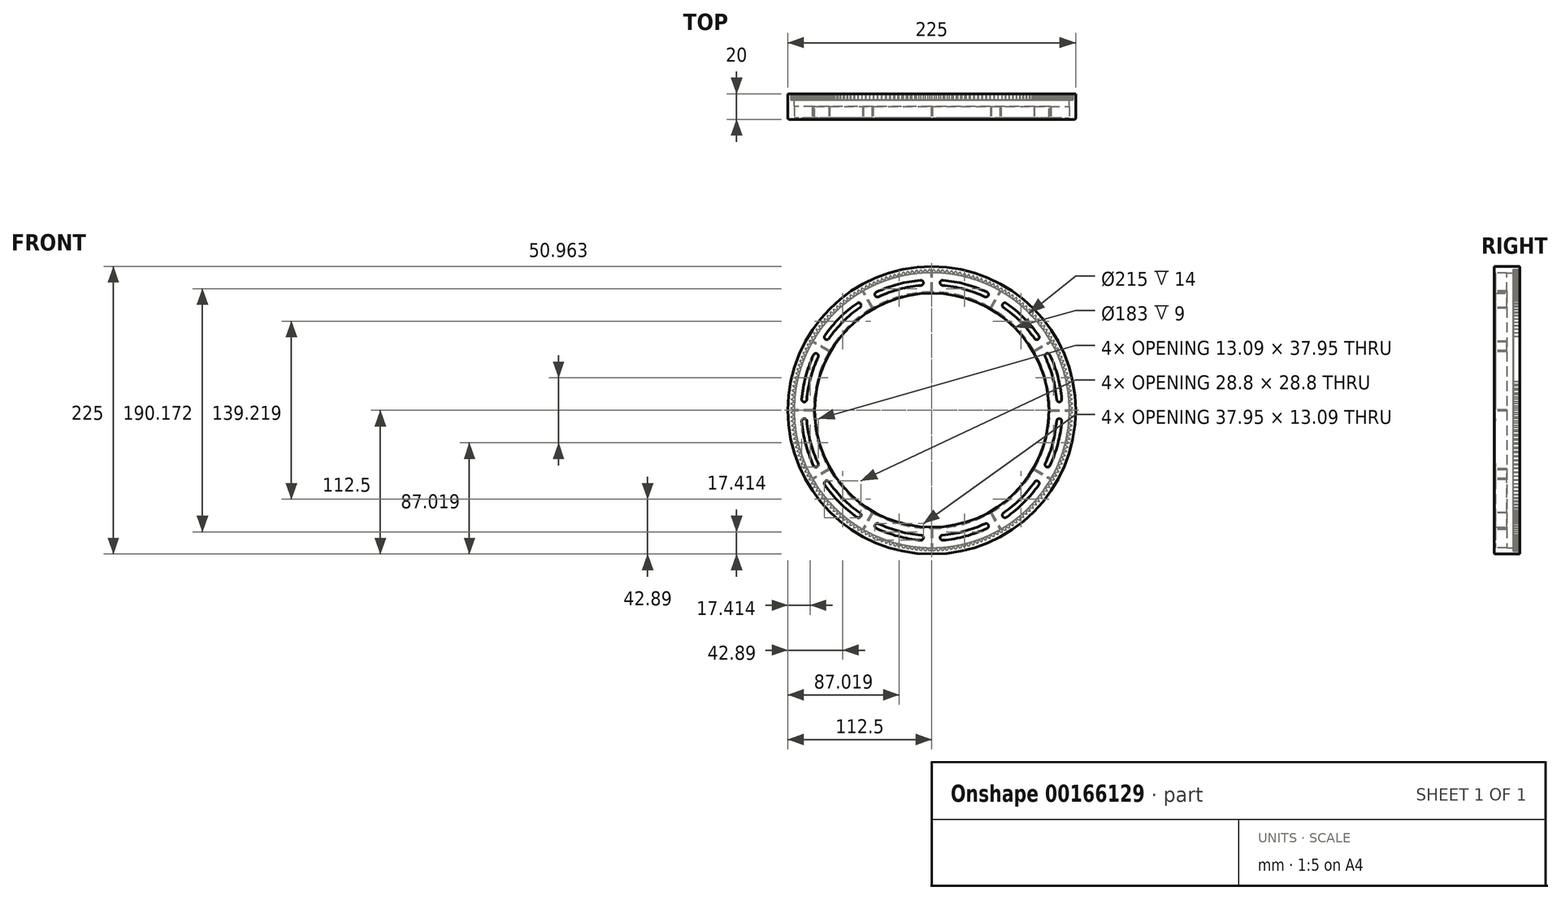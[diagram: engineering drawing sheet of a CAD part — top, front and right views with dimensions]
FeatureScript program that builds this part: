
annotation { "Feature Type Name" : "Feature", "Feature Type Description" : "" }
export const myFeature = defineFeature(function(context is Context, id is Id, definition is map)
    precondition{}
    {
        {
            var Q0;
            Q0=qCreatedBy(makeId("Top.planeOp"),FACE);
            var sketch = newSketch(context, id + "F0", { "sketchPlane" : qUnion([Q0])});
            skLineSegment(sketch, "E0", {"start": v(0, 14) * mm, "end": v(0, 0) * mm});
            skLineSegment(sketch, "E1", {"start": v(0, 14) * mm, "end": v(5, 14) * mm});
            skLineSegment(sketch, "E2", {"start": v(5, 14) * mm, "end": v(5, 0) * mm});
            skLineSegment(sketch, "E3", {"start": v(5, 0) * mm, "end": v(20, 0) * mm});
            skLineSegment(sketch, "E4", {"start": v(20, 0) * mm, "end": v(20, 9) * mm});
            skLineSegment(sketch, "E5", {"start": v(20, 9) * mm, "end": v(21, 9) * mm});
            skLineSegment(sketch, "E6", {"start": v(21, 9) * mm, "end": v(21, 0) * mm});
            skArc(sketch, "E7", {"start": v(0, 0) * mm, "mid": v(0.3, -0.7) * mm, "end": v(1, -1) * mm});
            skLineSegment(sketch, "E8", {"start": v(1, -1) * mm, "end": v(20, -1) * mm});
            skArc(sketch, "E9", {"start": v(21, 0) * mm, "mid": v(20.7, -0.7) * mm, "end": v(20, -1) * mm});
            skLineSegment(sketch, "E10", {"start": v(112.5, 10) * mm, "end": v(112.5, 0) * mm});
            skSolve(sketch);
        }
        {
            var Q0;
            Q0=makeQuery(id+"F0.imprint","IMPRINT",FACE,{"disambiguationData":[TD([[makeQuery(id+"F0.imprint","IMPRINT",EDGE,{"derivedFrom":sQuery(id+"F0.wireOp",EDGE,"E0")}),1.0]])]});
            var Q1;
            Q1=sQuery(id+"F0.wireOp",EDGE,"E10");
            revolve(context, id + "F1", {"entities" : qUnion([Q0]), "axis" : qUnion([Q1]), "revolveType" : RevolveType.FULL});
        }
        {
            var Q0;
            Q0=makeQuery(id+"F1.opRevolve","SWEPT_FACE",FACE,{"disambiguationData":[OSD([sQuery(id+"F0.wireOp",EDGE,"E3")])]});
            var sketch = newSketch(context, id + "F2", { "sketchPlane" : qUnion([Q0])});
            skLineSegment(sketch, "E11", {"start": v(-20, -0.5) * mm, "end": v(-5, -0.5) * mm});
            skLineSegment(sketch, "E12", {"start": v(-20, 0.5) * mm, "end": v(-5, 0.5) * mm});
            skPoint(sketch, "E13.start.orphan", {"position": v(-20, 0) * mm});
            skLineSegment(sketch, "E14.1.0", {"start": v(-32.64, 46.68) * mm, "end": v(-19.65, 54.18) * mm});
            skLineSegment(sketch, "E14.1.1", {"start": v(-32.14, 45.82) * mm, "end": v(-19.15, 53.32) * mm});
            skLineSegment(sketch, "E14.2.0", {"start": v(-66.68, 80.36) * mm, "end": v(-59.18, 93.35) * mm});
            skLineSegment(sketch, "E14.2.1", {"start": v(-65.82, 79.86) * mm, "end": v(-58.32, 92.85) * mm});
            skLineSegment(sketch, "E14.3.0", {"start": v(-113, 92.5) * mm, "end": v(-113, 107.5) * mm});
            skLineSegment(sketch, "E14.3.1", {"start": v(-112, 92.5) * mm, "end": v(-112, 107.5) * mm});
            skLineSegment(sketch, "E14.4.0", {"start": v(-159.18, 79.86) * mm, "end": v(-166.68, 92.85) * mm});
            skLineSegment(sketch, "E14.4.1", {"start": v(-158.32, 80.36) * mm, "end": v(-165.82, 93.35) * mm});
            skLineSegment(sketch, "E14.5.0", {"start": v(-192.86, 45.82) * mm, "end": v(-205.85, 53.32) * mm});
            skLineSegment(sketch, "E14.5.1", {"start": v(-192.36, 46.68) * mm, "end": v(-205.35, 54.18) * mm});
            skLineSegment(sketch, "E14.6.0", {"start": v(-205, -0.5) * mm, "end": v(-220, -0.5) * mm});
            skLineSegment(sketch, "E14.6.1", {"start": v(-205, 0.5) * mm, "end": v(-220, 0.5) * mm});
            skLineSegment(sketch, "E14.7.0", {"start": v(-192.36, -46.68) * mm, "end": v(-205.35, -54.18) * mm});
            skLineSegment(sketch, "E14.7.1", {"start": v(-192.86, -45.82) * mm, "end": v(-205.85, -53.32) * mm});
            skLineSegment(sketch, "E14.8.0", {"start": v(-158.32, -80.36) * mm, "end": v(-165.82, -93.35) * mm});
            skLineSegment(sketch, "E14.8.1", {"start": v(-159.18, -79.86) * mm, "end": v(-166.68, -92.85) * mm});
            skLineSegment(sketch, "E14.9.0", {"start": v(-112, -92.5) * mm, "end": v(-112, -107.5) * mm});
            skLineSegment(sketch, "E14.9.1", {"start": v(-113, -92.5) * mm, "end": v(-113, -107.5) * mm});
            skLineSegment(sketch, "E14.10.0", {"start": v(-65.82, -79.86) * mm, "end": v(-58.32, -92.85) * mm});
            skLineSegment(sketch, "E14.10.1", {"start": v(-66.68, -80.36) * mm, "end": v(-59.18, -93.35) * mm});
            skLineSegment(sketch, "E14.11.0", {"start": v(-32.14, -45.82) * mm, "end": v(-19.15, -53.32) * mm});
            skLineSegment(sketch, "E14.11.1", {"start": v(-32.64, -46.68) * mm, "end": v(-19.65, -54.18) * mm});
            skPoint(sketch, "E14.center", {"position": v(-112.5, 0) * mm});
            skArc(sketch, "E15.0.startCap", {"start": v(-210.15, 8.33) * mm, "mid": v(-212.3, 6.5) * mm, "end": v(-214.13, 8.67) * mm});
            skArc(sketch, "E15.0.endCap", {"start": v(-204.85, 43.3) * mm, "mid": v(-202.19, 44.27) * mm, "end": v(-201.23, 41.6) * mm});
            skArc(sketch, "E15.0.left", {"start": v(-214.13, 8.67) * mm, "mid": v(-211.02, 26.4) * mm, "end": v(-204.85, 43.3) * mm});
            skArc(sketch, "E15.0.right", {"start": v(-210.15, 8.33) * mm, "mid": v(-207.16, 25.36) * mm, "end": v(-201.23, 41.6) * mm});
            skArc(sketch, "E16.1.0", {"start": v(-201.23, -41.6) * mm, "mid": v(-207.16, -25.36) * mm, "end": v(-210.15, -8.33) * mm});
            skArc(sketch, "E16.1.1", {"start": v(-201.23, -41.6) * mm, "mid": v(-202.19, -44.27) * mm, "end": v(-204.85, -43.3) * mm});
            skArc(sketch, "E16.1.2", {"start": v(-204.85, -43.3) * mm, "mid": v(-211.02, -26.4) * mm, "end": v(-214.13, -8.67) * mm});
            skArc(sketch, "E16.1.3", {"start": v(-214.13, -8.67) * mm, "mid": v(-212.3, -6.5) * mm, "end": v(-210.15, -8.33) * mm});
            skArc(sketch, "E16.2.0", {"start": v(-168.54, -80.4) * mm, "mid": v(-181.8, -69.3) * mm, "end": v(-192.9, -56.04) * mm});
            skArc(sketch, "E16.2.1", {"start": v(-168.54, -80.4) * mm, "mid": v(-168.04, -83.18) * mm, "end": v(-170.82, -83.68) * mm});
            skArc(sketch, "E16.2.2", {"start": v(-170.82, -83.68) * mm, "mid": v(-184.62, -72.12) * mm, "end": v(-196.18, -58.32) * mm});
            skArc(sketch, "E16.2.3", {"start": v(-196.18, -58.32) * mm, "mid": v(-195.68, -55.54) * mm, "end": v(-192.9, -56.04) * mm});
            skArc(sketch, "E16.3.0", {"start": v(-120.83, -97.65) * mm, "mid": v(-137.86, -94.66) * mm, "end": v(-154.1, -88.73) * mm});
            skArc(sketch, "E16.3.1", {"start": v(-120.83, -97.65) * mm, "mid": v(-119, -99.8) * mm, "end": v(-121.17, -101.63) * mm});
            skArc(sketch, "E16.3.2", {"start": v(-121.17, -101.63) * mm, "mid": v(-138.9, -98.52) * mm, "end": v(-155.8, -92.35) * mm});
            skArc(sketch, "E16.3.3", {"start": v(-155.8, -92.35) * mm, "mid": v(-156.77, -89.69) * mm, "end": v(-154.1, -88.73) * mm});
            skArc(sketch, "E16.4.0", {"start": v(-70.9, -88.73) * mm, "mid": v(-87.14, -94.66) * mm, "end": v(-104.17, -97.65) * mm});
            skArc(sketch, "E16.4.1", {"start": v(-70.9, -88.73) * mm, "mid": v(-68.23, -89.69) * mm, "end": v(-69.2, -92.35) * mm});
            skArc(sketch, "E16.4.2", {"start": v(-69.2, -92.35) * mm, "mid": v(-86.1, -98.52) * mm, "end": v(-103.83, -101.63) * mm});
            skArc(sketch, "E16.4.3", {"start": v(-103.83, -101.63) * mm, "mid": v(-106, -99.8) * mm, "end": v(-104.17, -97.65) * mm});
            skArc(sketch, "E16.5.0", {"start": v(-32.1, -56.04) * mm, "mid": v(-43.2, -69.3) * mm, "end": v(-56.46, -80.4) * mm});
            skArc(sketch, "E16.5.1", {"start": v(-32.1, -56.04) * mm, "mid": v(-29.32, -55.54) * mm, "end": v(-28.82, -58.32) * mm});
            skArc(sketch, "E16.5.2", {"start": v(-28.82, -58.32) * mm, "mid": v(-40.38, -72.12) * mm, "end": v(-54.18, -83.68) * mm});
            skArc(sketch, "E16.5.3", {"start": v(-54.18, -83.68) * mm, "mid": v(-56.96, -83.18) * mm, "end": v(-56.46, -80.4) * mm});
            skArc(sketch, "E16.6.0", {"start": v(-14.85, -8.33) * mm, "mid": v(-17.84, -25.36) * mm, "end": v(-23.77, -41.6) * mm});
            skArc(sketch, "E16.6.1", {"start": v(-14.85, -8.33) * mm, "mid": v(-12.7, -6.5) * mm, "end": v(-10.87, -8.67) * mm});
            skArc(sketch, "E16.6.2", {"start": v(-10.87, -8.67) * mm, "mid": v(-13.98, -26.4) * mm, "end": v(-20.15, -43.3) * mm});
            skArc(sketch, "E16.6.3", {"start": v(-20.15, -43.3) * mm, "mid": v(-22.81, -44.27) * mm, "end": v(-23.77, -41.6) * mm});
            skArc(sketch, "E16.7.0", {"start": v(-23.77, 41.6) * mm, "mid": v(-17.84, 25.36) * mm, "end": v(-14.85, 8.33) * mm});
            skArc(sketch, "E16.7.1", {"start": v(-23.77, 41.6) * mm, "mid": v(-22.81, 44.27) * mm, "end": v(-20.15, 43.3) * mm});
            skArc(sketch, "E16.7.2", {"start": v(-20.15, 43.3) * mm, "mid": v(-13.98, 26.4) * mm, "end": v(-10.87, 8.67) * mm});
            skArc(sketch, "E16.7.3", {"start": v(-10.87, 8.67) * mm, "mid": v(-12.7, 6.5) * mm, "end": v(-14.85, 8.33) * mm});
            skArc(sketch, "E16.8.0", {"start": v(-56.46, 80.4) * mm, "mid": v(-43.2, 69.3) * mm, "end": v(-32.1, 56.04) * mm});
            skArc(sketch, "E16.8.1", {"start": v(-56.46, 80.4) * mm, "mid": v(-56.96, 83.18) * mm, "end": v(-54.18, 83.68) * mm});
            skArc(sketch, "E16.8.2", {"start": v(-54.18, 83.68) * mm, "mid": v(-40.38, 72.12) * mm, "end": v(-28.82, 58.32) * mm});
            skArc(sketch, "E16.8.3", {"start": v(-28.82, 58.32) * mm, "mid": v(-29.32, 55.54) * mm, "end": v(-32.1, 56.04) * mm});
            skArc(sketch, "E16.9.0", {"start": v(-104.17, 97.65) * mm, "mid": v(-87.14, 94.66) * mm, "end": v(-70.9, 88.73) * mm});
            skArc(sketch, "E16.9.1", {"start": v(-104.17, 97.65) * mm, "mid": v(-106, 99.8) * mm, "end": v(-103.83, 101.63) * mm});
            skArc(sketch, "E16.9.2", {"start": v(-103.83, 101.63) * mm, "mid": v(-86.1, 98.52) * mm, "end": v(-69.2, 92.35) * mm});
            skArc(sketch, "E16.9.3", {"start": v(-69.2, 92.35) * mm, "mid": v(-68.23, 89.69) * mm, "end": v(-70.9, 88.73) * mm});
            skArc(sketch, "E16.10.0", {"start": v(-154.1, 88.73) * mm, "mid": v(-137.86, 94.66) * mm, "end": v(-120.83, 97.65) * mm});
            skArc(sketch, "E16.10.1", {"start": v(-154.1, 88.73) * mm, "mid": v(-156.77, 89.69) * mm, "end": v(-155.8, 92.35) * mm});
            skArc(sketch, "E16.10.2", {"start": v(-155.8, 92.35) * mm, "mid": v(-138.9, 98.52) * mm, "end": v(-121.17, 101.63) * mm});
            skArc(sketch, "E16.10.3", {"start": v(-121.17, 101.63) * mm, "mid": v(-119, 99.8) * mm, "end": v(-120.83, 97.65) * mm});
            skArc(sketch, "E16.11.0", {"start": v(-192.9, 56.04) * mm, "mid": v(-181.8, 69.3) * mm, "end": v(-168.54, 80.4) * mm});
            skArc(sketch, "E16.11.1", {"start": v(-192.9, 56.04) * mm, "mid": v(-195.68, 55.54) * mm, "end": v(-196.18, 58.32) * mm});
            skArc(sketch, "E16.11.2", {"start": v(-196.18, 58.32) * mm, "mid": v(-184.62, 72.12) * mm, "end": v(-170.82, 83.68) * mm});
            skArc(sketch, "E16.11.3", {"start": v(-170.82, 83.68) * mm, "mid": v(-168.04, 83.18) * mm, "end": v(-168.54, 80.4) * mm});
            skSolve(sketch);
        }
        {
            var Q0;
            {var subQ0=sQuery(id+"F2.wireOp",EDGE,"E14.11.0");Q0=makeQuery(id+"F2.imprint","IMPRINT",FACE,{"disambiguationData":[TD([[makeQuery(id+"F2.imprint","IMPRINT",EDGE,{"derivedFrom":subQ0}),-1.0]])]});}
            var Q1;
            {var subQ0=sQuery(id+"F2.wireOp",EDGE,"E14.10.0");Q1=makeQuery(id+"F2.imprint","IMPRINT",FACE,{"disambiguationData":[TD([[makeQuery(id+"F2.imprint","IMPRINT",EDGE,{"derivedFrom":subQ0}),-1.0]])]});}
            var Q2;
            {var subQ0=sQuery(id+"F2.wireOp",EDGE,"E14.9.0");Q2=makeQuery(id+"F2.imprint","IMPRINT",FACE,{"disambiguationData":[TD([[makeQuery(id+"F2.imprint","IMPRINT",EDGE,{"derivedFrom":subQ0}),-1.0]])]});}
            var Q3;
            {var subQ0=sQuery(id+"F2.wireOp",EDGE,"E14.8.0");Q3=makeQuery(id+"F2.imprint","IMPRINT",FACE,{"disambiguationData":[TD([[makeQuery(id+"F2.imprint","IMPRINT",EDGE,{"derivedFrom":subQ0}),-1.0]])]});}
            var Q4;
            {var subQ0=sQuery(id+"F2.wireOp",EDGE,"E14.7.0");Q4=makeQuery(id+"F2.imprint","IMPRINT",FACE,{"disambiguationData":[TD([[makeQuery(id+"F2.imprint","IMPRINT",EDGE,{"derivedFrom":subQ0}),-1.0]])]});}
            var Q5;
            {var subQ0=sQuery(id+"F2.wireOp",EDGE,"E14.6.0");Q5=makeQuery(id+"F2.imprint","IMPRINT",FACE,{"disambiguationData":[TD([[makeQuery(id+"F2.imprint","IMPRINT",EDGE,{"derivedFrom":subQ0}),-1.0]])]});}
            var Q6;
            {var subQ0=sQuery(id+"F2.wireOp",EDGE,"E14.5.0");Q6=makeQuery(id+"F2.imprint","IMPRINT",FACE,{"disambiguationData":[TD([[makeQuery(id+"F2.imprint","IMPRINT",EDGE,{"derivedFrom":subQ0}),-1.0]])]});}
            var Q7;
            {var subQ0=sQuery(id+"F2.wireOp",EDGE,"E14.4.0");Q7=makeQuery(id+"F2.imprint","IMPRINT",FACE,{"disambiguationData":[TD([[makeQuery(id+"F2.imprint","IMPRINT",EDGE,{"derivedFrom":subQ0}),-1.0]])]});}
            var Q8;
            {var subQ0=sQuery(id+"F2.wireOp",EDGE,"E14.3.0");Q8=makeQuery(id+"F2.imprint","IMPRINT",FACE,{"disambiguationData":[TD([[makeQuery(id+"F2.imprint","IMPRINT",EDGE,{"derivedFrom":subQ0}),-1.0]])]});}
            var Q9;
            {var subQ0=sQuery(id+"F2.wireOp",EDGE,"E14.2.0");Q9=makeQuery(id+"F2.imprint","IMPRINT",FACE,{"disambiguationData":[TD([[makeQuery(id+"F2.imprint","IMPRINT",EDGE,{"derivedFrom":subQ0}),-1.0]])]});}
            var Q10;
            {var subQ0=sQuery(id+"F2.wireOp",EDGE,"E14.1.0");Q10=makeQuery(id+"F2.imprint","IMPRINT",FACE,{"disambiguationData":[TD([[makeQuery(id+"F2.imprint","IMPRINT",EDGE,{"derivedFrom":subQ0}),-1.0]])]});}
            var Q11;
            {var subQ0=sQuery(id+"F2.wireOp",EDGE,"E11");Q11=makeQuery(id+"F2.imprint","IMPRINT",FACE,{"disambiguationData":[TD([[makeQuery(id+"F2.imprint","IMPRINT",EDGE,{"derivedFrom":subQ0}),1.0]])]});}
            var Q12;
            Q12=sQuery(id+"F2.wireOp",EDGE,"E14.11.0");
            var Q13;
            Q13=sQuery(id+"F2.wireOp",EDGE,"E14.11.1");
            extrude(context, id + "F3", {"entities" : qUnion([Q0, Q1, Q2, Q3, Q4, Q5, Q6, Q7, Q8, Q9, Q10, Q11]), "operationType" : NewBodyOperationType.ADD, "surfaceEntities" : qUnion([Q12, Q13]), "depth" : 9 * mm});
        }
        {
            var Q0;
            Q0=makeQuery(id+"F1.opRevolve","SWEPT_FACE",FACE,{"disambiguationData":[OSD([sQuery(id+"F0.wireOp",EDGE,"E1")])]});
            var sketch = newSketch(context, id + "F4", { "sketchPlane" : qUnion([Q0])});
            skCircle(sketch, "E17", {"center": v(-112.5, 0) * mm, "radius": 112.5 * mm});
            skLineSegment(sketch, "E18", {"start": v(-222.6, 1.56) * mm, "end": v(-220.29, 0.17) * mm});
            skLineSegment(sketch, "E19", {"start": v(-220.29, -0.17) * mm, "end": v(-222.6, -1.56) * mm});
            skLineSegment(sketch, "E20.1.0", {"start": v(-222.6, -1.9) * mm, "end": v(-220.24, -3.21) * mm});
            skLineSegment(sketch, "E20.1.1", {"start": v(-220.23, -3.56) * mm, "end": v(-222.79, -5.2) * mm});
            skLineSegment(sketch, "E20.2.0", {"start": v(-222.79, -5.2) * mm, "end": v(-219.79, -6.75) * mm});
            skLineSegment(sketch, "E20.2.1", {"start": v(-219.79, -6.75) * mm, "end": v(-222.57, -8.66) * mm});
            skLineSegment(sketch, "E20.3.0", {"start": v(-222.57, -8.66) * mm, "end": v(-219.52, -10.12) * mm});
            skLineSegment(sketch, "E20.3.1", {"start": v(-219.52, -10.12) * mm, "end": v(-222.24, -12.12) * mm});
            skLineSegment(sketch, "E20.4.0", {"start": v(-222.24, -12.12) * mm, "end": v(-219.15, -13.47) * mm});
            skLineSegment(sketch, "E20.4.1", {"start": v(-219.15, -13.47) * mm, "end": v(-221.8, -15.56) * mm});
            skLineSegment(sketch, "E20.5.0", {"start": v(-221.8, -15.56) * mm, "end": v(-218.68, -16.82) * mm});
            skLineSegment(sketch, "E20.5.1", {"start": v(-218.68, -16.82) * mm, "end": v(-221.27, -18.98) * mm});
            skLineSegment(sketch, "E20.6.0", {"start": v(-221.27, -18.98) * mm, "end": v(-218.1, -20.14) * mm});
            skLineSegment(sketch, "E20.6.1", {"start": v(-218.1, -20.14) * mm, "end": v(-220.62, -22.4) * mm});
            skLineSegment(sketch, "E20.7.0", {"start": v(-220.62, -22.4) * mm, "end": v(-217.41, -23.45) * mm});
            skLineSegment(sketch, "E20.7.1", {"start": v(-217.41, -23.45) * mm, "end": v(-219.86, -25.78) * mm});
            skLineSegment(sketch, "E20.8.0", {"start": v(-219.86, -25.78) * mm, "end": v(-216.62, -26.73) * mm});
            skLineSegment(sketch, "E20.8.1", {"start": v(-216.62, -26.73) * mm, "end": v(-219, -29.13) * mm});
            skLineSegment(sketch, "E20.9.0", {"start": v(-219, -29.13) * mm, "end": v(-215.73, -30) * mm});
            skLineSegment(sketch, "E20.9.1", {"start": v(-215.73, -30) * mm, "end": v(-218.03, -32.47) * mm});
            skLineSegment(sketch, "E20.10.0", {"start": v(-218.03, -32.47) * mm, "end": v(-214.74, -33.22) * mm});
            skLineSegment(sketch, "E20.10.1", {"start": v(-214.74, -33.22) * mm, "end": v(-216.96, -35.76) * mm});
            skLineSegment(sketch, "E20.11.0", {"start": v(-216.96, -35.76) * mm, "end": v(-213.64, -36.41) * mm});
            skLineSegment(sketch, "E20.11.1", {"start": v(-213.64, -36.41) * mm, "end": v(-215.78, -39.03) * mm});
            skLineSegment(sketch, "E20.12.0", {"start": v(-215.78, -39.03) * mm, "end": v(-212.45, -39.57) * mm});
            skLineSegment(sketch, "E20.12.1", {"start": v(-212.45, -39.57) * mm, "end": v(-214.5, -42.25) * mm});
            skLineSegment(sketch, "E20.13.0", {"start": v(-214.5, -42.25) * mm, "end": v(-211.16, -42.7) * mm});
            skLineSegment(sketch, "E20.13.1", {"start": v(-211.16, -42.7) * mm, "end": v(-213.13, -45.44) * mm});
            skLineSegment(sketch, "E20.14.0", {"start": v(-213.13, -45.44) * mm, "end": v(-209.77, -45.77) * mm});
            skLineSegment(sketch, "E20.14.1", {"start": v(-209.77, -45.77) * mm, "end": v(-211.65, -48.57) * mm});
            skLineSegment(sketch, "E20.15.0", {"start": v(-211.65, -48.57) * mm, "end": v(-208.28, -48.8) * mm});
            skLineSegment(sketch, "E20.15.1", {"start": v(-208.28, -48.8) * mm, "end": v(-210.08, -51.66) * mm});
            skLineSegment(sketch, "E20.16.0", {"start": v(-210.08, -51.66) * mm, "end": v(-206.7, -51.79) * mm});
            skLineSegment(sketch, "E20.16.1", {"start": v(-206.7, -51.79) * mm, "end": v(-208.4, -54.7) * mm});
            skLineSegment(sketch, "E20.17.0", {"start": v(-208.4, -54.7) * mm, "end": v(-205.03, -54.72) * mm});
            skLineSegment(sketch, "E20.17.1", {"start": v(-205.03, -54.72) * mm, "end": v(-206.64, -57.69) * mm});
            skLineSegment(sketch, "E20.18.0", {"start": v(-206.64, -57.69) * mm, "end": v(-203.27, -57.6) * mm});
            skLineSegment(sketch, "E20.18.1", {"start": v(-203.27, -57.6) * mm, "end": v(-204.78, -60.62) * mm});
            skLineSegment(sketch, "E20.19.0", {"start": v(-204.78, -60.62) * mm, "end": v(-201.41, -60.42) * mm});
            skLineSegment(sketch, "E20.19.1", {"start": v(-201.41, -60.42) * mm, "end": v(-202.83, -63.49) * mm});
            skLineSegment(sketch, "E20.20.0", {"start": v(-202.83, -63.49) * mm, "end": v(-199.47, -63.19) * mm});
            skLineSegment(sketch, "E20.20.1", {"start": v(-199.47, -63.19) * mm, "end": v(-200.8, -66.3) * mm});
            skLineSegment(sketch, "E20.21.0", {"start": v(-200.8, -66.3) * mm, "end": v(-197.44, -65.89) * mm});
            skLineSegment(sketch, "E20.21.1", {"start": v(-197.44, -65.89) * mm, "end": v(-198.67, -69.03) * mm});
            skLineSegment(sketch, "E20.22.0", {"start": v(-198.67, -69.03) * mm, "end": v(-195.33, -68.52) * mm});
            skLineSegment(sketch, "E20.22.1", {"start": v(-195.33, -68.52) * mm, "end": v(-196.46, -71.7) * mm});
            skLineSegment(sketch, "E20.23.0", {"start": v(-196.46, -71.7) * mm, "end": v(-193.14, -71.1) * mm});
            skLineSegment(sketch, "E20.23.1", {"start": v(-193.14, -71.1) * mm, "end": v(-194.16, -74.3) * mm});
            skLineSegment(sketch, "E20.24.0", {"start": v(-194.16, -74.3) * mm, "end": v(-190.86, -73.59) * mm});
            skLineSegment(sketch, "E20.24.1", {"start": v(-190.86, -73.59) * mm, "end": v(-191.79, -76.84) * mm});
            skLineSegment(sketch, "E20.25.0", {"start": v(-191.79, -76.84) * mm, "end": v(-188.51, -76.01) * mm});
            skLineSegment(sketch, "E20.25.1", {"start": v(-188.51, -76.01) * mm, "end": v(-189.34, -79.29) * mm});
            skLineSegment(sketch, "E20.26.0", {"start": v(-189.34, -79.29) * mm, "end": v(-186.09, -78.36) * mm});
            skLineSegment(sketch, "E20.26.1", {"start": v(-186.09, -78.36) * mm, "end": v(-186.8, -81.66) * mm});
            skLineSegment(sketch, "E20.27.0", {"start": v(-186.8, -81.66) * mm, "end": v(-183.6, -80.64) * mm});
            skLineSegment(sketch, "E20.27.1", {"start": v(-183.6, -80.64) * mm, "end": v(-184.2, -83.96) * mm});
            skLineSegment(sketch, "E20.28.0", {"start": v(-184.2, -83.96) * mm, "end": v(-181.02, -82.83) * mm});
            skLineSegment(sketch, "E20.28.1", {"start": v(-181.02, -82.83) * mm, "end": v(-181.53, -86.17) * mm});
            skLineSegment(sketch, "E20.29.0", {"start": v(-181.53, -86.17) * mm, "end": v(-178.39, -84.94) * mm});
            skLineSegment(sketch, "E20.29.1", {"start": v(-178.39, -84.94) * mm, "end": v(-178.8, -88.3) * mm});
            skLineSegment(sketch, "E20.30.0", {"start": v(-178.8, -88.3) * mm, "end": v(-175.69, -86.97) * mm});
            skLineSegment(sketch, "E20.30.1", {"start": v(-175.69, -86.97) * mm, "end": v(-175.99, -90.33) * mm});
            skLineSegment(sketch, "E20.31.0", {"start": v(-175.99, -90.33) * mm, "end": v(-172.92, -88.91) * mm});
            skLineSegment(sketch, "E20.31.1", {"start": v(-172.92, -88.91) * mm, "end": v(-173.12, -92.28) * mm});
            skLineSegment(sketch, "E20.32.0", {"start": v(-173.12, -92.28) * mm, "end": v(-170.1, -90.77) * mm});
            skLineSegment(sketch, "E20.32.1", {"start": v(-170.1, -90.77) * mm, "end": v(-170.19, -94.14) * mm});
            skLineSegment(sketch, "E20.33.0", {"start": v(-170.19, -94.14) * mm, "end": v(-167.22, -92.53) * mm});
            skLineSegment(sketch, "E20.33.1", {"start": v(-167.22, -92.53) * mm, "end": v(-167.2, -95.9) * mm});
            skLineSegment(sketch, "E20.34.0", {"start": v(-167.2, -95.9) * mm, "end": v(-164.29, -94.2) * mm});
            skLineSegment(sketch, "E20.34.1", {"start": v(-164.29, -94.2) * mm, "end": v(-164.16, -97.58) * mm});
            skLineSegment(sketch, "E20.35.0", {"start": v(-164.16, -97.58) * mm, "end": v(-161.3, -95.78) * mm});
            skLineSegment(sketch, "E20.35.1", {"start": v(-161.3, -95.78) * mm, "end": v(-161.07, -99.15) * mm});
            skLineSegment(sketch, "E20.36.0", {"start": v(-161.07, -99.15) * mm, "end": v(-158.27, -97.27) * mm});
            skLineSegment(sketch, "E20.36.1", {"start": v(-158.27, -97.27) * mm, "end": v(-157.94, -100.63) * mm});
            skLineSegment(sketch, "E20.37.0", {"start": v(-157.94, -100.63) * mm, "end": v(-155.2, -98.66) * mm});
            skLineSegment(sketch, "E20.37.1", {"start": v(-155.2, -98.66) * mm, "end": v(-154.75, -102) * mm});
            skLineSegment(sketch, "E20.38.0", {"start": v(-154.75, -102) * mm, "end": v(-152.07, -99.95) * mm});
            skLineSegment(sketch, "E20.38.1", {"start": v(-152.07, -99.95) * mm, "end": v(-151.53, -103.28) * mm});
            skLineSegment(sketch, "E20.39.0", {"start": v(-151.53, -103.28) * mm, "end": v(-148.91, -101.14) * mm});
            skLineSegment(sketch, "E20.39.1", {"start": v(-148.91, -101.14) * mm, "end": v(-148.26, -104.46) * mm});
            skLineSegment(sketch, "E20.40.0", {"start": v(-148.26, -104.46) * mm, "end": v(-145.72, -102.24) * mm});
            skLineSegment(sketch, "E20.40.1", {"start": v(-145.72, -102.24) * mm, "end": v(-144.97, -105.53) * mm});
            skLineSegment(sketch, "E20.41.0", {"start": v(-144.97, -105.53) * mm, "end": v(-142.5, -103.23) * mm});
            skLineSegment(sketch, "E20.41.1", {"start": v(-142.5, -103.23) * mm, "end": v(-141.63, -106.5) * mm});
            skLineSegment(sketch, "E20.42.0", {"start": v(-141.63, -106.5) * mm, "end": v(-139.23, -104.12) * mm});
            skLineSegment(sketch, "E20.42.1", {"start": v(-139.23, -104.12) * mm, "end": v(-138.28, -107.36) * mm});
            skLineSegment(sketch, "E20.43.0", {"start": v(-138.28, -107.36) * mm, "end": v(-135.95, -104.91) * mm});
            skLineSegment(sketch, "E20.43.1", {"start": v(-135.95, -104.91) * mm, "end": v(-134.9, -108.12) * mm});
            skLineSegment(sketch, "E20.44.0", {"start": v(-134.9, -108.12) * mm, "end": v(-132.64, -105.6) * mm});
            skLineSegment(sketch, "E20.44.1", {"start": v(-132.64, -105.6) * mm, "end": v(-131.48, -108.77) * mm});
            skLineSegment(sketch, "E20.45.0", {"start": v(-131.48, -108.77) * mm, "end": v(-129.32, -106.18) * mm});
            skLineSegment(sketch, "E20.45.1", {"start": v(-129.32, -106.18) * mm, "end": v(-128.06, -109.3) * mm});
            skLineSegment(sketch, "E20.46.0", {"start": v(-128.06, -109.3) * mm, "end": v(-125.97, -106.65) * mm});
            skLineSegment(sketch, "E20.46.1", {"start": v(-125.97, -106.65) * mm, "end": v(-124.62, -109.74) * mm});
            skLineSegment(sketch, "E20.47.0", {"start": v(-124.62, -109.74) * mm, "end": v(-122.62, -107.02) * mm});
            skLineSegment(sketch, "E20.47.1", {"start": v(-122.62, -107.02) * mm, "end": v(-121.16, -110.07) * mm});
            skLineSegment(sketch, "E20.48.0", {"start": v(-121.16, -110.07) * mm, "end": v(-119.25, -107.29) * mm});
            skLineSegment(sketch, "E20.48.1", {"start": v(-119.25, -107.29) * mm, "end": v(-117.7, -110.29) * mm});
            skLineSegment(sketch, "E20.49.0", {"start": v(-117.7, -110.29) * mm, "end": v(-115.88, -107.45) * mm});
            skLineSegment(sketch, "E20.49.1", {"start": v(-115.88, -107.45) * mm, "end": v(-114.23, -110.4) * mm});
            skLineSegment(sketch, "E20.50.0", {"start": v(-114.23, -110.4) * mm, "end": v(-112.5, -107.5) * mm});
            skLineSegment(sketch, "E20.50.1", {"start": v(-112.5, -107.5) * mm, "end": v(-110.77, -110.4) * mm});
            skLineSegment(sketch, "E20.51.0", {"start": v(-110.77, -110.4) * mm, "end": v(-109.12, -107.45) * mm});
            skLineSegment(sketch, "E20.51.1", {"start": v(-109.12, -107.45) * mm, "end": v(-107.3, -110.29) * mm});
            skLineSegment(sketch, "E20.52.0", {"start": v(-107.3, -110.29) * mm, "end": v(-105.75, -107.29) * mm});
            skLineSegment(sketch, "E20.52.1", {"start": v(-105.75, -107.29) * mm, "end": v(-103.84, -110.07) * mm});
            skLineSegment(sketch, "E20.53.0", {"start": v(-103.84, -110.07) * mm, "end": v(-102.38, -107.02) * mm});
            skLineSegment(sketch, "E20.53.1", {"start": v(-102.38, -107.02) * mm, "end": v(-100.38, -109.74) * mm});
            skLineSegment(sketch, "E20.54.0", {"start": v(-100.38, -109.74) * mm, "end": v(-99.03, -106.65) * mm});
            skLineSegment(sketch, "E20.54.1", {"start": v(-99.03, -106.65) * mm, "end": v(-96.94, -109.3) * mm});
            skLineSegment(sketch, "E20.55.0", {"start": v(-96.94, -109.3) * mm, "end": v(-95.68, -106.18) * mm});
            skLineSegment(sketch, "E20.55.1", {"start": v(-95.68, -106.18) * mm, "end": v(-93.52, -108.77) * mm});
            skLineSegment(sketch, "E20.56.0", {"start": v(-93.52, -108.77) * mm, "end": v(-92.36, -105.6) * mm});
            skLineSegment(sketch, "E20.56.1", {"start": v(-92.36, -105.6) * mm, "end": v(-90.1, -108.12) * mm});
            skLineSegment(sketch, "E20.57.0", {"start": v(-90.1, -108.12) * mm, "end": v(-89.05, -104.91) * mm});
            skLineSegment(sketch, "E20.57.1", {"start": v(-89.05, -104.91) * mm, "end": v(-86.72, -107.36) * mm});
            skLineSegment(sketch, "E20.58.0", {"start": v(-86.72, -107.36) * mm, "end": v(-85.77, -104.12) * mm});
            skLineSegment(sketch, "E20.58.1", {"start": v(-85.77, -104.12) * mm, "end": v(-83.37, -106.5) * mm});
            skLineSegment(sketch, "E20.59.0", {"start": v(-83.37, -106.5) * mm, "end": v(-82.5, -103.23) * mm});
            skLineSegment(sketch, "E20.59.1", {"start": v(-82.5, -103.23) * mm, "end": v(-80.03, -105.53) * mm});
            skLineSegment(sketch, "E20.60.0", {"start": v(-80.03, -105.53) * mm, "end": v(-79.28, -102.24) * mm});
            skLineSegment(sketch, "E20.60.1", {"start": v(-79.28, -102.24) * mm, "end": v(-76.74, -104.46) * mm});
            skLineSegment(sketch, "E20.61.0", {"start": v(-76.74, -104.46) * mm, "end": v(-76.09, -101.14) * mm});
            skLineSegment(sketch, "E20.61.1", {"start": v(-76.09, -101.14) * mm, "end": v(-73.47, -103.28) * mm});
            skLineSegment(sketch, "E20.62.0", {"start": v(-73.47, -103.28) * mm, "end": v(-72.93, -99.95) * mm});
            skLineSegment(sketch, "E20.62.1", {"start": v(-72.93, -99.95) * mm, "end": v(-70.25, -102) * mm});
            skLineSegment(sketch, "E20.63.0", {"start": v(-70.25, -102) * mm, "end": v(-69.8, -98.66) * mm});
            skLineSegment(sketch, "E20.63.1", {"start": v(-69.8, -98.66) * mm, "end": v(-67.06, -100.63) * mm});
            skLineSegment(sketch, "E20.64.0", {"start": v(-67.06, -100.63) * mm, "end": v(-66.73, -97.27) * mm});
            skLineSegment(sketch, "E20.64.1", {"start": v(-66.73, -97.27) * mm, "end": v(-63.93, -99.15) * mm});
            skLineSegment(sketch, "E20.65.0", {"start": v(-63.93, -99.15) * mm, "end": v(-63.7, -95.78) * mm});
            skLineSegment(sketch, "E20.65.1", {"start": v(-63.7, -95.78) * mm, "end": v(-60.84, -97.58) * mm});
            skLineSegment(sketch, "E20.66.0", {"start": v(-60.84, -97.58) * mm, "end": v(-60.71, -94.2) * mm});
            skLineSegment(sketch, "E20.66.1", {"start": v(-60.71, -94.2) * mm, "end": v(-57.8, -95.9) * mm});
            skLineSegment(sketch, "E20.67.0", {"start": v(-57.8, -95.9) * mm, "end": v(-57.78, -92.53) * mm});
            skLineSegment(sketch, "E20.67.1", {"start": v(-57.78, -92.53) * mm, "end": v(-54.81, -94.14) * mm});
            skLineSegment(sketch, "E20.68.0", {"start": v(-54.81, -94.14) * mm, "end": v(-54.9, -90.77) * mm});
            skLineSegment(sketch, "E20.68.1", {"start": v(-54.9, -90.77) * mm, "end": v(-51.88, -92.28) * mm});
            skLineSegment(sketch, "E20.69.0", {"start": v(-51.88, -92.28) * mm, "end": v(-52.08, -88.91) * mm});
            skLineSegment(sketch, "E20.69.1", {"start": v(-52.08, -88.91) * mm, "end": v(-49.01, -90.33) * mm});
            skLineSegment(sketch, "E20.70.0", {"start": v(-49.01, -90.33) * mm, "end": v(-49.31, -86.97) * mm});
            skLineSegment(sketch, "E20.70.1", {"start": v(-49.31, -86.97) * mm, "end": v(-46.2, -88.3) * mm});
            skLineSegment(sketch, "E20.71.0", {"start": v(-46.2, -88.3) * mm, "end": v(-46.61, -84.94) * mm});
            skLineSegment(sketch, "E20.71.1", {"start": v(-46.61, -84.94) * mm, "end": v(-43.47, -86.17) * mm});
            skLineSegment(sketch, "E20.72.0", {"start": v(-43.47, -86.17) * mm, "end": v(-43.98, -82.83) * mm});
            skLineSegment(sketch, "E20.72.1", {"start": v(-43.98, -82.83) * mm, "end": v(-40.8, -83.96) * mm});
            skLineSegment(sketch, "E20.73.0", {"start": v(-40.8, -83.96) * mm, "end": v(-41.4, -80.64) * mm});
            skLineSegment(sketch, "E20.73.1", {"start": v(-41.4, -80.64) * mm, "end": v(-38.2, -81.66) * mm});
            skLineSegment(sketch, "E20.74.0", {"start": v(-38.2, -81.66) * mm, "end": v(-38.91, -78.36) * mm});
            skLineSegment(sketch, "E20.74.1", {"start": v(-38.91, -78.36) * mm, "end": v(-35.66, -79.29) * mm});
            skLineSegment(sketch, "E20.75.0", {"start": v(-35.66, -79.29) * mm, "end": v(-36.49, -76.01) * mm});
            skLineSegment(sketch, "E20.75.1", {"start": v(-36.49, -76.01) * mm, "end": v(-33.21, -76.84) * mm});
            skLineSegment(sketch, "E20.76.0", {"start": v(-33.21, -76.84) * mm, "end": v(-34.14, -73.59) * mm});
            skLineSegment(sketch, "E20.76.1", {"start": v(-34.14, -73.59) * mm, "end": v(-30.84, -74.3) * mm});
            skLineSegment(sketch, "E20.77.0", {"start": v(-30.84, -74.3) * mm, "end": v(-31.86, -71.1) * mm});
            skLineSegment(sketch, "E20.77.1", {"start": v(-31.86, -71.1) * mm, "end": v(-28.54, -71.7) * mm});
            skLineSegment(sketch, "E20.78.0", {"start": v(-28.54, -71.7) * mm, "end": v(-29.67, -68.52) * mm});
            skLineSegment(sketch, "E20.78.1", {"start": v(-29.67, -68.52) * mm, "end": v(-26.33, -69.03) * mm});
            skLineSegment(sketch, "E20.79.0", {"start": v(-26.33, -69.03) * mm, "end": v(-27.56, -65.89) * mm});
            skLineSegment(sketch, "E20.79.1", {"start": v(-27.56, -65.89) * mm, "end": v(-24.2, -66.3) * mm});
            skLineSegment(sketch, "E20.80.0", {"start": v(-24.2, -66.3) * mm, "end": v(-25.53, -63.19) * mm});
            skLineSegment(sketch, "E20.80.1", {"start": v(-25.53, -63.19) * mm, "end": v(-22.17, -63.49) * mm});
            skLineSegment(sketch, "E20.81.0", {"start": v(-22.17, -63.49) * mm, "end": v(-23.59, -60.42) * mm});
            skLineSegment(sketch, "E20.81.1", {"start": v(-23.59, -60.42) * mm, "end": v(-20.22, -60.62) * mm});
            skLineSegment(sketch, "E20.82.0", {"start": v(-20.22, -60.62) * mm, "end": v(-21.73, -57.6) * mm});
            skLineSegment(sketch, "E20.82.1", {"start": v(-21.73, -57.6) * mm, "end": v(-18.36, -57.69) * mm});
            skLineSegment(sketch, "E20.83.0", {"start": v(-18.36, -57.69) * mm, "end": v(-19.97, -54.72) * mm});
            skLineSegment(sketch, "E20.83.1", {"start": v(-19.97, -54.72) * mm, "end": v(-16.6, -54.7) * mm});
            skLineSegment(sketch, "E20.84.0", {"start": v(-16.6, -54.7) * mm, "end": v(-18.3, -51.79) * mm});
            skLineSegment(sketch, "E20.84.1", {"start": v(-18.3, -51.79) * mm, "end": v(-14.92, -51.66) * mm});
            skLineSegment(sketch, "E20.85.0", {"start": v(-14.92, -51.66) * mm, "end": v(-16.72, -48.8) * mm});
            skLineSegment(sketch, "E20.85.1", {"start": v(-16.72, -48.8) * mm, "end": v(-13.35, -48.57) * mm});
            skLineSegment(sketch, "E20.86.0", {"start": v(-13.35, -48.57) * mm, "end": v(-15.23, -45.77) * mm});
            skLineSegment(sketch, "E20.86.1", {"start": v(-15.23, -45.77) * mm, "end": v(-11.87, -45.44) * mm});
            skLineSegment(sketch, "E20.87.0", {"start": v(-11.87, -45.44) * mm, "end": v(-13.84, -42.7) * mm});
            skLineSegment(sketch, "E20.87.1", {"start": v(-13.84, -42.7) * mm, "end": v(-10.5, -42.25) * mm});
            skLineSegment(sketch, "E20.88.0", {"start": v(-10.5, -42.25) * mm, "end": v(-12.55, -39.57) * mm});
            skLineSegment(sketch, "E20.88.1", {"start": v(-12.55, -39.57) * mm, "end": v(-9.22, -39.03) * mm});
            skLineSegment(sketch, "E20.89.0", {"start": v(-9.22, -39.03) * mm, "end": v(-11.36, -36.41) * mm});
            skLineSegment(sketch, "E20.89.1", {"start": v(-11.36, -36.41) * mm, "end": v(-8.04, -35.76) * mm});
            skLineSegment(sketch, "E20.90.0", {"start": v(-8.04, -35.76) * mm, "end": v(-10.26, -33.22) * mm});
            skLineSegment(sketch, "E20.90.1", {"start": v(-10.26, -33.22) * mm, "end": v(-6.97, -32.47) * mm});
            skLineSegment(sketch, "E20.91.0", {"start": v(-6.97, -32.47) * mm, "end": v(-9.27, -30) * mm});
            skLineSegment(sketch, "E20.91.1", {"start": v(-9.27, -30) * mm, "end": v(-6, -29.13) * mm});
            skLineSegment(sketch, "E20.92.0", {"start": v(-6, -29.13) * mm, "end": v(-8.38, -26.73) * mm});
            skLineSegment(sketch, "E20.92.1", {"start": v(-8.38, -26.73) * mm, "end": v(-5.14, -25.78) * mm});
            skLineSegment(sketch, "E20.93.0", {"start": v(-5.14, -25.78) * mm, "end": v(-7.59, -23.45) * mm});
            skLineSegment(sketch, "E20.93.1", {"start": v(-7.59, -23.45) * mm, "end": v(-4.38, -22.4) * mm});
            skLineSegment(sketch, "E20.94.0", {"start": v(-4.38, -22.4) * mm, "end": v(-6.9, -20.14) * mm});
            skLineSegment(sketch, "E20.94.1", {"start": v(-6.9, -20.14) * mm, "end": v(-3.73, -18.98) * mm});
            skLineSegment(sketch, "E20.95.0", {"start": v(-3.73, -18.98) * mm, "end": v(-6.32, -16.82) * mm});
            skLineSegment(sketch, "E20.95.1", {"start": v(-6.32, -16.82) * mm, "end": v(-3.2, -15.56) * mm});
            skLineSegment(sketch, "E20.96.0", {"start": v(-3.2, -15.56) * mm, "end": v(-5.85, -13.47) * mm});
            skLineSegment(sketch, "E20.96.1", {"start": v(-5.85, -13.47) * mm, "end": v(-2.76, -12.12) * mm});
            skLineSegment(sketch, "E20.97.0", {"start": v(-2.76, -12.12) * mm, "end": v(-5.48, -10.12) * mm});
            skLineSegment(sketch, "E20.97.1", {"start": v(-5.48, -10.12) * mm, "end": v(-2.43, -8.66) * mm});
            skLineSegment(sketch, "E20.98.0", {"start": v(-2.43, -8.66) * mm, "end": v(-5.21, -6.75) * mm});
            skLineSegment(sketch, "E20.98.1", {"start": v(-5.21, -6.75) * mm, "end": v(-2.21, -5.2) * mm});
            skLineSegment(sketch, "E20.99.0", {"start": v(-2.21, -5.2) * mm, "end": v(-5.05, -3.38) * mm});
            skLineSegment(sketch, "E20.99.1", {"start": v(-5.05, -3.38) * mm, "end": v(-2.1, -1.73) * mm});
            skLineSegment(sketch, "E20.100.0", {"start": v(-2.1, -1.73) * mm, "end": v(-5, 0) * mm});
            skLineSegment(sketch, "E20.100.1", {"start": v(-5, 0) * mm, "end": v(-2.1, 1.73) * mm});
            skLineSegment(sketch, "E20.101.0", {"start": v(-2.1, 1.73) * mm, "end": v(-5.05, 3.38) * mm});
            skLineSegment(sketch, "E20.101.1", {"start": v(-5.05, 3.38) * mm, "end": v(-2.21, 5.2) * mm});
            skLineSegment(sketch, "E20.102.0", {"start": v(-2.21, 5.2) * mm, "end": v(-5.21, 6.75) * mm});
            skLineSegment(sketch, "E20.102.1", {"start": v(-5.21, 6.75) * mm, "end": v(-2.43, 8.66) * mm});
            skLineSegment(sketch, "E20.103.0", {"start": v(-2.43, 8.66) * mm, "end": v(-5.48, 10.12) * mm});
            skLineSegment(sketch, "E20.103.1", {"start": v(-5.48, 10.12) * mm, "end": v(-2.76, 12.12) * mm});
            skLineSegment(sketch, "E20.104.0", {"start": v(-2.76, 12.12) * mm, "end": v(-5.85, 13.47) * mm});
            skLineSegment(sketch, "E20.104.1", {"start": v(-5.85, 13.47) * mm, "end": v(-3.2, 15.56) * mm});
            skLineSegment(sketch, "E20.105.0", {"start": v(-3.2, 15.56) * mm, "end": v(-6.32, 16.82) * mm});
            skLineSegment(sketch, "E20.105.1", {"start": v(-6.32, 16.82) * mm, "end": v(-3.73, 18.98) * mm});
            skLineSegment(sketch, "E20.106.0", {"start": v(-3.73, 18.98) * mm, "end": v(-6.9, 20.14) * mm});
            skLineSegment(sketch, "E20.106.1", {"start": v(-6.9, 20.14) * mm, "end": v(-4.38, 22.4) * mm});
            skLineSegment(sketch, "E20.107.0", {"start": v(-4.38, 22.4) * mm, "end": v(-7.59, 23.45) * mm});
            skLineSegment(sketch, "E20.107.1", {"start": v(-7.59, 23.45) * mm, "end": v(-5.14, 25.78) * mm});
            skLineSegment(sketch, "E20.108.0", {"start": v(-5.14, 25.78) * mm, "end": v(-8.38, 26.73) * mm});
            skLineSegment(sketch, "E20.108.1", {"start": v(-8.38, 26.73) * mm, "end": v(-6, 29.13) * mm});
            skLineSegment(sketch, "E20.109.0", {"start": v(-6, 29.13) * mm, "end": v(-9.27, 30) * mm});
            skLineSegment(sketch, "E20.109.1", {"start": v(-9.27, 30) * mm, "end": v(-6.97, 32.47) * mm});
            skLineSegment(sketch, "E20.110.0", {"start": v(-6.97, 32.47) * mm, "end": v(-10.26, 33.22) * mm});
            skLineSegment(sketch, "E20.110.1", {"start": v(-10.26, 33.22) * mm, "end": v(-8.04, 35.76) * mm});
            skLineSegment(sketch, "E20.111.0", {"start": v(-8.04, 35.76) * mm, "end": v(-11.36, 36.41) * mm});
            skLineSegment(sketch, "E20.111.1", {"start": v(-11.36, 36.41) * mm, "end": v(-9.22, 39.03) * mm});
            skLineSegment(sketch, "E20.112.0", {"start": v(-9.22, 39.03) * mm, "end": v(-12.55, 39.57) * mm});
            skLineSegment(sketch, "E20.112.1", {"start": v(-12.55, 39.57) * mm, "end": v(-10.5, 42.25) * mm});
            skLineSegment(sketch, "E20.113.0", {"start": v(-10.5, 42.25) * mm, "end": v(-13.84, 42.7) * mm});
            skLineSegment(sketch, "E20.113.1", {"start": v(-13.84, 42.7) * mm, "end": v(-11.87, 45.44) * mm});
            skLineSegment(sketch, "E20.114.0", {"start": v(-11.87, 45.44) * mm, "end": v(-15.23, 45.77) * mm});
            skLineSegment(sketch, "E20.114.1", {"start": v(-15.23, 45.77) * mm, "end": v(-13.35, 48.57) * mm});
            skLineSegment(sketch, "E20.115.0", {"start": v(-13.35, 48.57) * mm, "end": v(-16.72, 48.8) * mm});
            skLineSegment(sketch, "E20.115.1", {"start": v(-16.72, 48.8) * mm, "end": v(-14.92, 51.66) * mm});
            skLineSegment(sketch, "E20.116.0", {"start": v(-14.92, 51.66) * mm, "end": v(-18.3, 51.79) * mm});
            skLineSegment(sketch, "E20.116.1", {"start": v(-18.3, 51.79) * mm, "end": v(-16.6, 54.7) * mm});
            skLineSegment(sketch, "E20.117.0", {"start": v(-16.6, 54.7) * mm, "end": v(-19.97, 54.72) * mm});
            skLineSegment(sketch, "E20.117.1", {"start": v(-19.97, 54.72) * mm, "end": v(-18.36, 57.69) * mm});
            skLineSegment(sketch, "E20.118.0", {"start": v(-18.36, 57.69) * mm, "end": v(-21.73, 57.6) * mm});
            skLineSegment(sketch, "E20.118.1", {"start": v(-21.73, 57.6) * mm, "end": v(-20.22, 60.62) * mm});
            skLineSegment(sketch, "E20.119.0", {"start": v(-20.22, 60.62) * mm, "end": v(-23.59, 60.42) * mm});
            skLineSegment(sketch, "E20.119.1", {"start": v(-23.59, 60.42) * mm, "end": v(-22.17, 63.49) * mm});
            skLineSegment(sketch, "E20.120.0", {"start": v(-22.17, 63.49) * mm, "end": v(-25.53, 63.19) * mm});
            skLineSegment(sketch, "E20.120.1", {"start": v(-25.53, 63.19) * mm, "end": v(-24.2, 66.3) * mm});
            skLineSegment(sketch, "E20.121.0", {"start": v(-24.2, 66.3) * mm, "end": v(-27.56, 65.89) * mm});
            skLineSegment(sketch, "E20.121.1", {"start": v(-27.56, 65.89) * mm, "end": v(-26.33, 69.03) * mm});
            skLineSegment(sketch, "E20.122.0", {"start": v(-26.33, 69.03) * mm, "end": v(-29.67, 68.52) * mm});
            skLineSegment(sketch, "E20.122.1", {"start": v(-29.67, 68.52) * mm, "end": v(-28.54, 71.7) * mm});
            skLineSegment(sketch, "E20.123.0", {"start": v(-28.54, 71.7) * mm, "end": v(-31.86, 71.1) * mm});
            skLineSegment(sketch, "E20.123.1", {"start": v(-31.86, 71.1) * mm, "end": v(-30.84, 74.3) * mm});
            skLineSegment(sketch, "E20.124.0", {"start": v(-30.84, 74.3) * mm, "end": v(-34.14, 73.59) * mm});
            skLineSegment(sketch, "E20.124.1", {"start": v(-34.14, 73.59) * mm, "end": v(-33.21, 76.84) * mm});
            skLineSegment(sketch, "E20.125.0", {"start": v(-33.21, 76.84) * mm, "end": v(-36.49, 76.01) * mm});
            skLineSegment(sketch, "E20.125.1", {"start": v(-36.49, 76.01) * mm, "end": v(-35.66, 79.29) * mm});
            skLineSegment(sketch, "E20.126.0", {"start": v(-35.66, 79.29) * mm, "end": v(-38.91, 78.36) * mm});
            skLineSegment(sketch, "E20.126.1", {"start": v(-38.91, 78.36) * mm, "end": v(-38.2, 81.66) * mm});
            skLineSegment(sketch, "E20.127.0", {"start": v(-38.2, 81.66) * mm, "end": v(-41.4, 80.64) * mm});
            skLineSegment(sketch, "E20.127.1", {"start": v(-41.4, 80.64) * mm, "end": v(-40.8, 83.96) * mm});
            skLineSegment(sketch, "E20.128.0", {"start": v(-40.8, 83.96) * mm, "end": v(-43.98, 82.83) * mm});
            skLineSegment(sketch, "E20.128.1", {"start": v(-43.98, 82.83) * mm, "end": v(-43.47, 86.17) * mm});
            skLineSegment(sketch, "E20.129.0", {"start": v(-43.47, 86.17) * mm, "end": v(-46.61, 84.94) * mm});
            skLineSegment(sketch, "E20.129.1", {"start": v(-46.61, 84.94) * mm, "end": v(-46.2, 88.3) * mm});
            skLineSegment(sketch, "E20.130.0", {"start": v(-46.2, 88.3) * mm, "end": v(-49.31, 86.97) * mm});
            skLineSegment(sketch, "E20.130.1", {"start": v(-49.31, 86.97) * mm, "end": v(-49.01, 90.33) * mm});
            skLineSegment(sketch, "E20.131.0", {"start": v(-49.01, 90.33) * mm, "end": v(-52.08, 88.91) * mm});
            skLineSegment(sketch, "E20.131.1", {"start": v(-52.08, 88.91) * mm, "end": v(-51.88, 92.28) * mm});
            skLineSegment(sketch, "E20.132.0", {"start": v(-51.88, 92.28) * mm, "end": v(-54.9, 90.77) * mm});
            skLineSegment(sketch, "E20.132.1", {"start": v(-54.9, 90.77) * mm, "end": v(-54.81, 94.14) * mm});
            skLineSegment(sketch, "E20.133.0", {"start": v(-54.81, 94.14) * mm, "end": v(-57.78, 92.53) * mm});
            skLineSegment(sketch, "E20.133.1", {"start": v(-57.78, 92.53) * mm, "end": v(-57.8, 95.9) * mm});
            skLineSegment(sketch, "E20.134.0", {"start": v(-57.8, 95.9) * mm, "end": v(-60.71, 94.2) * mm});
            skLineSegment(sketch, "E20.134.1", {"start": v(-60.71, 94.2) * mm, "end": v(-60.84, 97.58) * mm});
            skLineSegment(sketch, "E20.135.0", {"start": v(-60.84, 97.58) * mm, "end": v(-63.7, 95.78) * mm});
            skLineSegment(sketch, "E20.135.1", {"start": v(-63.7, 95.78) * mm, "end": v(-63.93, 99.15) * mm});
            skLineSegment(sketch, "E20.136.0", {"start": v(-63.93, 99.15) * mm, "end": v(-66.73, 97.27) * mm});
            skLineSegment(sketch, "E20.136.1", {"start": v(-66.73, 97.27) * mm, "end": v(-67.06, 100.63) * mm});
            skLineSegment(sketch, "E20.137.0", {"start": v(-67.06, 100.63) * mm, "end": v(-69.8, 98.66) * mm});
            skLineSegment(sketch, "E20.137.1", {"start": v(-69.8, 98.66) * mm, "end": v(-70.25, 102) * mm});
            skLineSegment(sketch, "E20.138.0", {"start": v(-70.25, 102) * mm, "end": v(-72.93, 99.95) * mm});
            skLineSegment(sketch, "E20.138.1", {"start": v(-72.93, 99.95) * mm, "end": v(-73.47, 103.28) * mm});
            skLineSegment(sketch, "E20.139.0", {"start": v(-73.47, 103.28) * mm, "end": v(-76.09, 101.14) * mm});
            skLineSegment(sketch, "E20.139.1", {"start": v(-76.09, 101.14) * mm, "end": v(-76.74, 104.46) * mm});
            skLineSegment(sketch, "E20.140.0", {"start": v(-76.74, 104.46) * mm, "end": v(-79.28, 102.24) * mm});
            skLineSegment(sketch, "E20.140.1", {"start": v(-79.28, 102.24) * mm, "end": v(-80.03, 105.53) * mm});
            skLineSegment(sketch, "E20.141.0", {"start": v(-80.03, 105.53) * mm, "end": v(-82.5, 103.23) * mm});
            skLineSegment(sketch, "E20.141.1", {"start": v(-82.5, 103.23) * mm, "end": v(-83.37, 106.5) * mm});
            skLineSegment(sketch, "E20.142.0", {"start": v(-83.37, 106.5) * mm, "end": v(-85.77, 104.12) * mm});
            skLineSegment(sketch, "E20.142.1", {"start": v(-85.77, 104.12) * mm, "end": v(-86.72, 107.36) * mm});
            skLineSegment(sketch, "E20.143.0", {"start": v(-86.72, 107.36) * mm, "end": v(-89.05, 104.91) * mm});
            skLineSegment(sketch, "E20.143.1", {"start": v(-89.05, 104.91) * mm, "end": v(-90.1, 108.12) * mm});
            skLineSegment(sketch, "E20.144.0", {"start": v(-90.1, 108.12) * mm, "end": v(-92.36, 105.6) * mm});
            skLineSegment(sketch, "E20.144.1", {"start": v(-92.36, 105.6) * mm, "end": v(-93.52, 108.77) * mm});
            skLineSegment(sketch, "E20.145.0", {"start": v(-93.52, 108.77) * mm, "end": v(-95.68, 106.18) * mm});
            skLineSegment(sketch, "E20.145.1", {"start": v(-95.68, 106.18) * mm, "end": v(-96.94, 109.3) * mm});
            skLineSegment(sketch, "E20.146.0", {"start": v(-96.94, 109.3) * mm, "end": v(-99.03, 106.65) * mm});
            skLineSegment(sketch, "E20.146.1", {"start": v(-99.03, 106.65) * mm, "end": v(-100.38, 109.74) * mm});
            skLineSegment(sketch, "E20.147.0", {"start": v(-100.38, 109.74) * mm, "end": v(-102.38, 107.02) * mm});
            skLineSegment(sketch, "E20.147.1", {"start": v(-102.38, 107.02) * mm, "end": v(-103.84, 110.07) * mm});
            skLineSegment(sketch, "E20.148.0", {"start": v(-103.84, 110.07) * mm, "end": v(-105.75, 107.29) * mm});
            skLineSegment(sketch, "E20.148.1", {"start": v(-105.75, 107.29) * mm, "end": v(-107.3, 110.29) * mm});
            skLineSegment(sketch, "E20.149.0", {"start": v(-107.3, 110.29) * mm, "end": v(-109.12, 107.45) * mm});
            skLineSegment(sketch, "E20.149.1", {"start": v(-109.12, 107.45) * mm, "end": v(-110.77, 110.4) * mm});
            skLineSegment(sketch, "E20.150.0", {"start": v(-110.77, 110.4) * mm, "end": v(-112.5, 107.5) * mm});
            skLineSegment(sketch, "E20.150.1", {"start": v(-112.5, 107.5) * mm, "end": v(-114.23, 110.4) * mm});
            skLineSegment(sketch, "E20.151.0", {"start": v(-114.23, 110.4) * mm, "end": v(-115.88, 107.45) * mm});
            skLineSegment(sketch, "E20.151.1", {"start": v(-115.88, 107.45) * mm, "end": v(-117.7, 110.29) * mm});
            skLineSegment(sketch, "E20.152.0", {"start": v(-117.7, 110.29) * mm, "end": v(-119.25, 107.29) * mm});
            skLineSegment(sketch, "E20.152.1", {"start": v(-119.25, 107.29) * mm, "end": v(-121.16, 110.07) * mm});
            skLineSegment(sketch, "E20.153.0", {"start": v(-121.16, 110.07) * mm, "end": v(-122.62, 107.02) * mm});
            skLineSegment(sketch, "E20.153.1", {"start": v(-122.62, 107.02) * mm, "end": v(-124.62, 109.74) * mm});
            skLineSegment(sketch, "E20.154.0", {"start": v(-124.62, 109.74) * mm, "end": v(-125.97, 106.65) * mm});
            skLineSegment(sketch, "E20.154.1", {"start": v(-125.97, 106.65) * mm, "end": v(-128.06, 109.3) * mm});
            skLineSegment(sketch, "E20.155.0", {"start": v(-128.06, 109.3) * mm, "end": v(-129.32, 106.18) * mm});
            skLineSegment(sketch, "E20.155.1", {"start": v(-129.32, 106.18) * mm, "end": v(-131.48, 108.77) * mm});
            skLineSegment(sketch, "E20.156.0", {"start": v(-131.48, 108.77) * mm, "end": v(-132.64, 105.6) * mm});
            skLineSegment(sketch, "E20.156.1", {"start": v(-132.64, 105.6) * mm, "end": v(-134.9, 108.12) * mm});
            skLineSegment(sketch, "E20.157.0", {"start": v(-134.9, 108.12) * mm, "end": v(-135.95, 104.91) * mm});
            skLineSegment(sketch, "E20.157.1", {"start": v(-135.95, 104.91) * mm, "end": v(-138.28, 107.36) * mm});
            skLineSegment(sketch, "E20.158.0", {"start": v(-138.28, 107.36) * mm, "end": v(-139.23, 104.12) * mm});
            skLineSegment(sketch, "E20.158.1", {"start": v(-139.23, 104.12) * mm, "end": v(-141.63, 106.5) * mm});
            skLineSegment(sketch, "E20.159.0", {"start": v(-141.63, 106.5) * mm, "end": v(-142.5, 103.23) * mm});
            skLineSegment(sketch, "E20.159.1", {"start": v(-142.5, 103.23) * mm, "end": v(-144.97, 105.53) * mm});
            skLineSegment(sketch, "E20.160.0", {"start": v(-144.97, 105.53) * mm, "end": v(-145.72, 102.24) * mm});
            skLineSegment(sketch, "E20.160.1", {"start": v(-145.72, 102.24) * mm, "end": v(-148.26, 104.46) * mm});
            skLineSegment(sketch, "E20.161.0", {"start": v(-148.26, 104.46) * mm, "end": v(-148.91, 101.14) * mm});
            skLineSegment(sketch, "E20.161.1", {"start": v(-148.91, 101.14) * mm, "end": v(-151.53, 103.28) * mm});
            skLineSegment(sketch, "E20.162.0", {"start": v(-151.53, 103.28) * mm, "end": v(-152.07, 99.95) * mm});
            skLineSegment(sketch, "E20.162.1", {"start": v(-152.07, 99.95) * mm, "end": v(-154.75, 102) * mm});
            skLineSegment(sketch, "E20.163.0", {"start": v(-154.75, 102) * mm, "end": v(-155.2, 98.66) * mm});
            skLineSegment(sketch, "E20.163.1", {"start": v(-155.2, 98.66) * mm, "end": v(-157.94, 100.63) * mm});
            skLineSegment(sketch, "E20.164.0", {"start": v(-157.94, 100.63) * mm, "end": v(-158.27, 97.27) * mm});
            skLineSegment(sketch, "E20.164.1", {"start": v(-158.27, 97.27) * mm, "end": v(-161.07, 99.15) * mm});
            skLineSegment(sketch, "E20.165.0", {"start": v(-161.07, 99.15) * mm, "end": v(-161.3, 95.78) * mm});
            skLineSegment(sketch, "E20.165.1", {"start": v(-161.3, 95.78) * mm, "end": v(-164.16, 97.58) * mm});
            skLineSegment(sketch, "E20.166.0", {"start": v(-164.16, 97.58) * mm, "end": v(-164.29, 94.2) * mm});
            skLineSegment(sketch, "E20.166.1", {"start": v(-164.29, 94.2) * mm, "end": v(-167.2, 95.9) * mm});
            skLineSegment(sketch, "E20.167.0", {"start": v(-167.2, 95.9) * mm, "end": v(-167.22, 92.53) * mm});
            skLineSegment(sketch, "E20.167.1", {"start": v(-167.22, 92.53) * mm, "end": v(-170.19, 94.14) * mm});
            skLineSegment(sketch, "E20.168.0", {"start": v(-170.19, 94.14) * mm, "end": v(-170.1, 90.77) * mm});
            skLineSegment(sketch, "E20.168.1", {"start": v(-170.1, 90.77) * mm, "end": v(-173.12, 92.28) * mm});
            skLineSegment(sketch, "E20.169.0", {"start": v(-173.12, 92.28) * mm, "end": v(-172.92, 88.91) * mm});
            skLineSegment(sketch, "E20.169.1", {"start": v(-172.92, 88.91) * mm, "end": v(-175.99, 90.33) * mm});
            skLineSegment(sketch, "E20.170.0", {"start": v(-175.99, 90.33) * mm, "end": v(-175.69, 86.97) * mm});
            skLineSegment(sketch, "E20.170.1", {"start": v(-175.69, 86.97) * mm, "end": v(-178.8, 88.3) * mm});
            skLineSegment(sketch, "E20.171.0", {"start": v(-178.8, 88.3) * mm, "end": v(-178.39, 84.94) * mm});
            skLineSegment(sketch, "E20.171.1", {"start": v(-178.39, 84.94) * mm, "end": v(-181.53, 86.17) * mm});
            skLineSegment(sketch, "E20.172.0", {"start": v(-181.53, 86.17) * mm, "end": v(-181.02, 82.83) * mm});
            skLineSegment(sketch, "E20.172.1", {"start": v(-181.02, 82.83) * mm, "end": v(-184.2, 83.96) * mm});
            skLineSegment(sketch, "E20.173.0", {"start": v(-184.2, 83.96) * mm, "end": v(-183.6, 80.64) * mm});
            skLineSegment(sketch, "E20.173.1", {"start": v(-183.6, 80.64) * mm, "end": v(-186.8, 81.66) * mm});
            skLineSegment(sketch, "E20.174.0", {"start": v(-186.8, 81.66) * mm, "end": v(-186.09, 78.36) * mm});
            skLineSegment(sketch, "E20.174.1", {"start": v(-186.09, 78.36) * mm, "end": v(-189.34, 79.29) * mm});
            skLineSegment(sketch, "E20.175.0", {"start": v(-189.34, 79.29) * mm, "end": v(-188.51, 76.01) * mm});
            skLineSegment(sketch, "E20.175.1", {"start": v(-188.51, 76.01) * mm, "end": v(-191.79, 76.84) * mm});
            skLineSegment(sketch, "E20.176.0", {"start": v(-191.79, 76.84) * mm, "end": v(-190.86, 73.59) * mm});
            skLineSegment(sketch, "E20.176.1", {"start": v(-190.86, 73.59) * mm, "end": v(-194.16, 74.3) * mm});
            skLineSegment(sketch, "E20.177.0", {"start": v(-194.16, 74.3) * mm, "end": v(-193.14, 71.1) * mm});
            skLineSegment(sketch, "E20.177.1", {"start": v(-193.14, 71.1) * mm, "end": v(-196.46, 71.7) * mm});
            skLineSegment(sketch, "E20.178.0", {"start": v(-196.46, 71.7) * mm, "end": v(-195.33, 68.52) * mm});
            skLineSegment(sketch, "E20.178.1", {"start": v(-195.33, 68.52) * mm, "end": v(-198.67, 69.03) * mm});
            skLineSegment(sketch, "E20.179.0", {"start": v(-198.67, 69.03) * mm, "end": v(-197.44, 65.89) * mm});
            skLineSegment(sketch, "E20.179.1", {"start": v(-197.44, 65.89) * mm, "end": v(-200.8, 66.3) * mm});
            skLineSegment(sketch, "E20.180.0", {"start": v(-200.8, 66.3) * mm, "end": v(-199.47, 63.19) * mm});
            skLineSegment(sketch, "E20.180.1", {"start": v(-199.47, 63.19) * mm, "end": v(-202.83, 63.49) * mm});
            skLineSegment(sketch, "E20.181.0", {"start": v(-202.83, 63.49) * mm, "end": v(-201.41, 60.42) * mm});
            skLineSegment(sketch, "E20.181.1", {"start": v(-201.41, 60.42) * mm, "end": v(-204.78, 60.62) * mm});
            skLineSegment(sketch, "E20.182.0", {"start": v(-204.78, 60.62) * mm, "end": v(-203.27, 57.6) * mm});
            skLineSegment(sketch, "E20.182.1", {"start": v(-203.27, 57.6) * mm, "end": v(-206.64, 57.69) * mm});
            skLineSegment(sketch, "E20.183.0", {"start": v(-206.64, 57.69) * mm, "end": v(-205.03, 54.72) * mm});
            skLineSegment(sketch, "E20.183.1", {"start": v(-205.03, 54.72) * mm, "end": v(-208.4, 54.7) * mm});
            skLineSegment(sketch, "E20.184.0", {"start": v(-208.4, 54.7) * mm, "end": v(-206.7, 51.79) * mm});
            skLineSegment(sketch, "E20.184.1", {"start": v(-206.7, 51.79) * mm, "end": v(-210.08, 51.66) * mm});
            skLineSegment(sketch, "E20.185.0", {"start": v(-210.08, 51.66) * mm, "end": v(-208.28, 48.8) * mm});
            skLineSegment(sketch, "E20.185.1", {"start": v(-208.28, 48.8) * mm, "end": v(-211.65, 48.57) * mm});
            skLineSegment(sketch, "E20.186.0", {"start": v(-211.65, 48.57) * mm, "end": v(-209.77, 45.77) * mm});
            skLineSegment(sketch, "E20.186.1", {"start": v(-209.77, 45.77) * mm, "end": v(-213.13, 45.44) * mm});
            skLineSegment(sketch, "E20.187.0", {"start": v(-213.13, 45.44) * mm, "end": v(-211.16, 42.7) * mm});
            skLineSegment(sketch, "E20.187.1", {"start": v(-211.16, 42.7) * mm, "end": v(-214.5, 42.25) * mm});
            skLineSegment(sketch, "E20.188.0", {"start": v(-214.5, 42.25) * mm, "end": v(-212.45, 39.57) * mm});
            skLineSegment(sketch, "E20.188.1", {"start": v(-212.45, 39.57) * mm, "end": v(-215.78, 39.03) * mm});
            skLineSegment(sketch, "E20.189.0", {"start": v(-215.78, 39.03) * mm, "end": v(-213.64, 36.41) * mm});
            skLineSegment(sketch, "E20.189.1", {"start": v(-213.64, 36.41) * mm, "end": v(-216.96, 35.76) * mm});
            skLineSegment(sketch, "E20.190.0", {"start": v(-216.96, 35.76) * mm, "end": v(-214.74, 33.22) * mm});
            skLineSegment(sketch, "E20.190.1", {"start": v(-214.74, 33.22) * mm, "end": v(-218.03, 32.47) * mm});
            skLineSegment(sketch, "E20.191.0", {"start": v(-218.03, 32.47) * mm, "end": v(-215.73, 30) * mm});
            skLineSegment(sketch, "E20.191.1", {"start": v(-215.73, 30) * mm, "end": v(-219, 29.13) * mm});
            skLineSegment(sketch, "E20.192.0", {"start": v(-219, 29.13) * mm, "end": v(-216.62, 26.73) * mm});
            skLineSegment(sketch, "E20.192.1", {"start": v(-216.62, 26.73) * mm, "end": v(-219.86, 25.78) * mm});
            skLineSegment(sketch, "E20.193.0", {"start": v(-219.86, 25.78) * mm, "end": v(-217.41, 23.45) * mm});
            skLineSegment(sketch, "E20.193.1", {"start": v(-217.41, 23.45) * mm, "end": v(-220.62, 22.4) * mm});
            skLineSegment(sketch, "E20.194.0", {"start": v(-220.62, 22.4) * mm, "end": v(-218.1, 20.14) * mm});
            skLineSegment(sketch, "E20.194.1", {"start": v(-218.1, 20.14) * mm, "end": v(-221.27, 18.98) * mm});
            skLineSegment(sketch, "E20.195.0", {"start": v(-221.27, 18.98) * mm, "end": v(-218.68, 16.82) * mm});
            skLineSegment(sketch, "E20.195.1", {"start": v(-218.68, 16.82) * mm, "end": v(-221.8, 15.56) * mm});
            skLineSegment(sketch, "E20.196.0", {"start": v(-221.8, 15.56) * mm, "end": v(-219.15, 13.47) * mm});
            skLineSegment(sketch, "E20.196.1", {"start": v(-219.15, 13.47) * mm, "end": v(-222.24, 12.12) * mm});
            skLineSegment(sketch, "E20.197.0", {"start": v(-222.24, 12.12) * mm, "end": v(-219.52, 10.12) * mm});
            skLineSegment(sketch, "E20.197.1", {"start": v(-219.52, 10.12) * mm, "end": v(-222.26, 8.81) * mm});
            skLineSegment(sketch, "E20.198.0", {"start": v(-222.29, 8.47) * mm, "end": v(-220.06, 6.94) * mm});
            skLineSegment(sketch, "E20.198.1", {"start": v(-220.08, 6.6) * mm, "end": v(-222.48, 5.36) * mm});
            skLineSegment(sketch, "E20.199.0", {"start": v(-222.5, 5.01) * mm, "end": v(-220.23, 3.56) * mm});
            skLineSegment(sketch, "E20.199.1", {"start": v(-220.24, 3.21) * mm, "end": v(-222.6, 1.9) * mm});
            skPoint(sketch, "E21.visualSharp", {"position": v(-222.9, 1.73) * mm});
            skArc(sketch, "E21.filletArc", {"start": v(-222.6, 1.9) * mm, "mid": v(-222.7, 1.73) * mm, "end": v(-222.6, 1.56) * mm});
            skPoint(sketch, "E22.visualSharp", {"position": v(-220, 0) * mm});
            skArc(sketch, "E22.filletArc", {"start": v(-220.29, -0.17) * mm, "mid": v(-220.19, 0) * mm, "end": v(-220.29, 0.17) * mm});
            skPoint(sketch, "E23.visualSharp", {"position": v(-219.95, -3.38) * mm});
            skArc(sketch, "E23.filletArc", {"start": v(-220.23, -3.56) * mm, "mid": v(-220.14, -3.38) * mm, "end": v(-220.24, -3.21) * mm});
            skPoint(sketch, "E24.visualSharp", {"position": v(-222.9, -1.73) * mm});
            skArc(sketch, "E24.filletArc", {"start": v(-222.6, -1.56) * mm, "mid": v(-222.7, -1.73) * mm, "end": v(-222.6, -1.9) * mm});
            skPoint(sketch, "E25.visualSharp", {"position": v(-219.95, 3.38) * mm});
            skArc(sketch, "E25.filletArc", {"start": v(-220.24, 3.21) * mm, "mid": v(-220.14, 3.38) * mm, "end": v(-220.23, 3.56) * mm});
            skPoint(sketch, "E26.visualSharp", {"position": v(-222.79, 5.2) * mm});
            skArc(sketch, "E26.filletArc", {"start": v(-222.48, 5.36) * mm, "mid": v(-222.59, 5.2) * mm, "end": v(-222.5, 5.01) * mm});
            skPoint(sketch, "E27.visualSharp", {"position": v(-219.79, 6.75) * mm});
            skArc(sketch, "E27.filletArc", {"start": v(-220.08, 6.6) * mm, "mid": v(-219.98, 6.76) * mm, "end": v(-220.06, 6.94) * mm});
            skPoint(sketch, "E28.visualSharp", {"position": v(-222.57, 8.66) * mm});
            skArc(sketch, "E28.filletArc", {"start": v(-222.26, 8.81) * mm, "mid": v(-222.37, 8.65) * mm, "end": v(-222.29, 8.47) * mm});
            skSolve(sketch);
        }
        {
            var Q0;
            Q0=makeQuery(id+"F4.imprint","IMPRINT",FACE,{"disambiguationData":[TD([[makeQuery(id+"F4.imprint","IMPRINT",EDGE,{"derivedFrom":sQuery(id+"F4.wireOp",EDGE,"E17")}),1.0]])]});
            extrude(context, id + "F5", {"entities" : qUnion([Q0]), "operationType" : NewBodyOperationType.ADD, "depth" : 5 * mm});
        }
        {
            var Q0;
            Q0=makeQuery(id+"F5.opExtrude","SWEPT_EDGE",EDGE,{"disambiguationData":[OSD([sQuery(id+"F0.wireOp",EDGE,"E1"),sQuery(id+"F0.wireOp",EDGE,"E2"),sQuery(id+"F4.wireOp",EDGE,"E20.197.0"),sQuery(id+"F4.wireOp",EDGE,"E20.197.1")])]});
            fillet(context, id + "F6", {"entities" : qUnion([Q0]), "radius" : .2 * mm, "tangentPropagation" : true, "allowEdgeOverflow" : false});
        }
        {
            var Q0;
            Q0=makeQuery(id+"F5.opExtrude","SWEPT_EDGE",EDGE,{"disambiguationData":[OSD([sQuery(id+"F0.wireOp",EDGE,"E1"),sQuery(id+"F0.wireOp",EDGE,"E2"),sQuery(id+"F4.wireOp",EDGE,"E20.196.0"),sQuery(id+"F4.wireOp",EDGE,"E20.196.1")])]});
            var Q1;
            Q1=makeQuery(id+"F5.opExtrude","SWEPT_EDGE",EDGE,{"disambiguationData":[OSD([sQuery(id+"F4.wireOp",EDGE,"E20.196.1"),sQuery(id+"F4.wireOp",EDGE,"E20.197.0")])]});
            var Q2;
            Q2=makeQuery(id+"F5.opExtrude","SWEPT_EDGE",EDGE,{"disambiguationData":[OSD([sQuery(id+"F4.wireOp",EDGE,"E20.195.1"),sQuery(id+"F4.wireOp",EDGE,"E20.196.0")])]});
            var Q3;
            Q3=makeQuery(id+"F5.opExtrude","SWEPT_EDGE",EDGE,{"disambiguationData":[OSD([sQuery(id+"F0.wireOp",EDGE,"E1"),sQuery(id+"F0.wireOp",EDGE,"E2"),sQuery(id+"F4.wireOp",EDGE,"E20.195.0"),sQuery(id+"F4.wireOp",EDGE,"E20.195.1")])]});
            var Q4;
            Q4=makeQuery(id+"F5.opExtrude","SWEPT_EDGE",EDGE,{"disambiguationData":[OSD([sQuery(id+"F4.wireOp",EDGE,"E20.194.1"),sQuery(id+"F4.wireOp",EDGE,"E20.195.0")])]});
            var Q5;
            Q5=makeQuery(id+"F5.opExtrude","SWEPT_EDGE",EDGE,{"disambiguationData":[OSD([sQuery(id+"F0.wireOp",EDGE,"E1"),sQuery(id+"F0.wireOp",EDGE,"E2"),sQuery(id+"F4.wireOp",EDGE,"E20.194.0"),sQuery(id+"F4.wireOp",EDGE,"E20.194.1")])]});
            var Q6;
            Q6=makeQuery(id+"F5.opExtrude","SWEPT_EDGE",EDGE,{"disambiguationData":[OSD([sQuery(id+"F4.wireOp",EDGE,"E20.193.1"),sQuery(id+"F4.wireOp",EDGE,"E20.194.0")])]});
            var Q7;
            Q7=makeQuery(id+"F5.opExtrude","SWEPT_EDGE",EDGE,{"disambiguationData":[OSD([sQuery(id+"F0.wireOp",EDGE,"E1"),sQuery(id+"F0.wireOp",EDGE,"E2"),sQuery(id+"F4.wireOp",EDGE,"E20.193.0"),sQuery(id+"F4.wireOp",EDGE,"E20.193.1")])]});
            var Q8;
            Q8=makeQuery(id+"F5.opExtrude","SWEPT_EDGE",EDGE,{"disambiguationData":[OSD([sQuery(id+"F4.wireOp",EDGE,"E20.192.1"),sQuery(id+"F4.wireOp",EDGE,"E20.193.0")])]});
            var Q9;
            Q9=makeQuery(id+"F5.opExtrude","SWEPT_EDGE",EDGE,{"disambiguationData":[OSD([sQuery(id+"F0.wireOp",EDGE,"E1"),sQuery(id+"F0.wireOp",EDGE,"E2"),sQuery(id+"F4.wireOp",EDGE,"E20.192.0"),sQuery(id+"F4.wireOp",EDGE,"E20.192.1")])]});
            var Q10;
            Q10=makeQuery(id+"F5.opExtrude","SWEPT_EDGE",EDGE,{"disambiguationData":[OSD([sQuery(id+"F4.wireOp",EDGE,"E20.191.1"),sQuery(id+"F4.wireOp",EDGE,"E20.192.0")])]});
            var Q11;
            Q11=makeQuery(id+"F5.opExtrude","SWEPT_EDGE",EDGE,{"disambiguationData":[OSD([sQuery(id+"F0.wireOp",EDGE,"E1"),sQuery(id+"F0.wireOp",EDGE,"E2"),sQuery(id+"F4.wireOp",EDGE,"E20.191.0"),sQuery(id+"F4.wireOp",EDGE,"E20.191.1")])]});
            var Q12;
            Q12=makeQuery(id+"F5.opExtrude","SWEPT_EDGE",EDGE,{"disambiguationData":[OSD([sQuery(id+"F4.wireOp",EDGE,"E20.190.1"),sQuery(id+"F4.wireOp",EDGE,"E20.191.0")])]});
            var Q13;
            Q13=makeQuery(id+"F5.opExtrude","SWEPT_EDGE",EDGE,{"disambiguationData":[OSD([sQuery(id+"F0.wireOp",EDGE,"E1"),sQuery(id+"F0.wireOp",EDGE,"E2"),sQuery(id+"F4.wireOp",EDGE,"E20.190.0"),sQuery(id+"F4.wireOp",EDGE,"E20.190.1")])]});
            var Q14;
            Q14=makeQuery(id+"F5.opExtrude","SWEPT_EDGE",EDGE,{"disambiguationData":[OSD([sQuery(id+"F4.wireOp",EDGE,"E20.189.1"),sQuery(id+"F4.wireOp",EDGE,"E20.190.0")])]});
            var Q15;
            Q15=makeQuery(id+"F5.opExtrude","SWEPT_EDGE",EDGE,{"disambiguationData":[OSD([sQuery(id+"F0.wireOp",EDGE,"E1"),sQuery(id+"F0.wireOp",EDGE,"E2"),sQuery(id+"F4.wireOp",EDGE,"E20.189.0"),sQuery(id+"F4.wireOp",EDGE,"E20.189.1")])]});
            var Q16;
            Q16=makeQuery(id+"F5.opExtrude","SWEPT_EDGE",EDGE,{"disambiguationData":[OSD([sQuery(id+"F4.wireOp",EDGE,"E20.188.1"),sQuery(id+"F4.wireOp",EDGE,"E20.189.0")])]});
            var Q17;
            Q17=makeQuery(id+"F5.opExtrude","SWEPT_EDGE",EDGE,{"disambiguationData":[OSD([sQuery(id+"F0.wireOp",EDGE,"E1"),sQuery(id+"F0.wireOp",EDGE,"E2"),sQuery(id+"F4.wireOp",EDGE,"E20.188.0"),sQuery(id+"F4.wireOp",EDGE,"E20.188.1")])]});
            var Q18;
            Q18=makeQuery(id+"F5.opExtrude","SWEPT_EDGE",EDGE,{"disambiguationData":[OSD([sQuery(id+"F4.wireOp",EDGE,"E20.187.1"),sQuery(id+"F4.wireOp",EDGE,"E20.188.0")])]});
            var Q19;
            Q19=makeQuery(id+"F5.opExtrude","SWEPT_EDGE",EDGE,{"disambiguationData":[OSD([sQuery(id+"F0.wireOp",EDGE,"E1"),sQuery(id+"F0.wireOp",EDGE,"E2"),sQuery(id+"F4.wireOp",EDGE,"E20.187.0"),sQuery(id+"F4.wireOp",EDGE,"E20.187.1")])]});
            var Q20;
            Q20=makeQuery(id+"F5.opExtrude","SWEPT_EDGE",EDGE,{"disambiguationData":[OSD([sQuery(id+"F4.wireOp",EDGE,"E20.186.1"),sQuery(id+"F4.wireOp",EDGE,"E20.187.0")])]});
            var Q21;
            Q21=makeQuery(id+"F5.opExtrude","SWEPT_EDGE",EDGE,{"disambiguationData":[OSD([sQuery(id+"F0.wireOp",EDGE,"E1"),sQuery(id+"F0.wireOp",EDGE,"E2"),sQuery(id+"F4.wireOp",EDGE,"E20.186.0"),sQuery(id+"F4.wireOp",EDGE,"E20.186.1")])]});
            var Q22;
            Q22=makeQuery(id+"F5.opExtrude","SWEPT_EDGE",EDGE,{"disambiguationData":[OSD([sQuery(id+"F4.wireOp",EDGE,"E20.185.1"),sQuery(id+"F4.wireOp",EDGE,"E20.186.0")])]});
            var Q23;
            Q23=makeQuery(id+"F5.opExtrude","SWEPT_EDGE",EDGE,{"disambiguationData":[OSD([sQuery(id+"F0.wireOp",EDGE,"E1"),sQuery(id+"F0.wireOp",EDGE,"E2"),sQuery(id+"F4.wireOp",EDGE,"E20.185.0"),sQuery(id+"F4.wireOp",EDGE,"E20.185.1")])]});
            var Q24;
            Q24=makeQuery(id+"F5.opExtrude","SWEPT_EDGE",EDGE,{"disambiguationData":[OSD([sQuery(id+"F4.wireOp",EDGE,"E20.184.1"),sQuery(id+"F4.wireOp",EDGE,"E20.185.0")])]});
            var Q25;
            Q25=makeQuery(id+"F5.opExtrude","SWEPT_EDGE",EDGE,{"disambiguationData":[OSD([sQuery(id+"F0.wireOp",EDGE,"E1"),sQuery(id+"F0.wireOp",EDGE,"E2"),sQuery(id+"F4.wireOp",EDGE,"E20.184.0"),sQuery(id+"F4.wireOp",EDGE,"E20.184.1")])]});
            var Q26;
            Q26=makeQuery(id+"F5.opExtrude","SWEPT_EDGE",EDGE,{"disambiguationData":[OSD([sQuery(id+"F4.wireOp",EDGE,"E20.183.1"),sQuery(id+"F4.wireOp",EDGE,"E20.184.0")])]});
            var Q27;
            Q27=makeQuery(id+"F5.opExtrude","SWEPT_EDGE",EDGE,{"disambiguationData":[OSD([sQuery(id+"F0.wireOp",EDGE,"E1"),sQuery(id+"F0.wireOp",EDGE,"E2"),sQuery(id+"F4.wireOp",EDGE,"E20.183.0"),sQuery(id+"F4.wireOp",EDGE,"E20.183.1")])]});
            var Q28;
            Q28=makeQuery(id+"F5.opExtrude","SWEPT_EDGE",EDGE,{"disambiguationData":[OSD([sQuery(id+"F4.wireOp",EDGE,"E20.182.1"),sQuery(id+"F4.wireOp",EDGE,"E20.183.0")])]});
            var Q29;
            Q29=makeQuery(id+"F5.opExtrude","SWEPT_EDGE",EDGE,{"disambiguationData":[OSD([sQuery(id+"F0.wireOp",EDGE,"E1"),sQuery(id+"F0.wireOp",EDGE,"E2"),sQuery(id+"F4.wireOp",EDGE,"E20.182.0"),sQuery(id+"F4.wireOp",EDGE,"E20.182.1")])]});
            var Q30;
            Q30=makeQuery(id+"F5.opExtrude","SWEPT_EDGE",EDGE,{"disambiguationData":[OSD([sQuery(id+"F4.wireOp",EDGE,"E20.181.1"),sQuery(id+"F4.wireOp",EDGE,"E20.182.0")])]});
            var Q31;
            Q31=makeQuery(id+"F5.opExtrude","SWEPT_EDGE",EDGE,{"disambiguationData":[OSD([sQuery(id+"F0.wireOp",EDGE,"E1"),sQuery(id+"F0.wireOp",EDGE,"E2"),sQuery(id+"F4.wireOp",EDGE,"E20.181.0"),sQuery(id+"F4.wireOp",EDGE,"E20.181.1")])]});
            var Q32;
            Q32=makeQuery(id+"F5.opExtrude","SWEPT_EDGE",EDGE,{"disambiguationData":[OSD([sQuery(id+"F4.wireOp",EDGE,"E20.179.1"),sQuery(id+"F4.wireOp",EDGE,"E20.180.0")])]});
            var Q33;
            Q33=makeQuery(id+"F5.opExtrude","SWEPT_EDGE",EDGE,{"disambiguationData":[OSD([sQuery(id+"F0.wireOp",EDGE,"E1"),sQuery(id+"F0.wireOp",EDGE,"E2"),sQuery(id+"F4.wireOp",EDGE,"E20.178.0"),sQuery(id+"F4.wireOp",EDGE,"E20.178.1")])]});
            var Q34;
            Q34=makeQuery(id+"F5.opExtrude","SWEPT_EDGE",EDGE,{"disambiguationData":[OSD([sQuery(id+"F0.wireOp",EDGE,"E1"),sQuery(id+"F0.wireOp",EDGE,"E2"),sQuery(id+"F4.wireOp",EDGE,"E20.177.0"),sQuery(id+"F4.wireOp",EDGE,"E20.177.1")])]});
            var Q35;
            Q35=makeQuery(id+"F5.opExtrude","SWEPT_EDGE",EDGE,{"disambiguationData":[OSD([sQuery(id+"F4.wireOp",EDGE,"E20.180.1"),sQuery(id+"F4.wireOp",EDGE,"E20.181.0")])]});
            var Q36;
            Q36=makeQuery(id+"F5.opExtrude","SWEPT_EDGE",EDGE,{"disambiguationData":[OSD([sQuery(id+"F0.wireOp",EDGE,"E1"),sQuery(id+"F0.wireOp",EDGE,"E2"),sQuery(id+"F4.wireOp",EDGE,"E20.180.0"),sQuery(id+"F4.wireOp",EDGE,"E20.180.1")])]});
            var Q37;
            Q37=makeQuery(id+"F5.opExtrude","SWEPT_EDGE",EDGE,{"disambiguationData":[OSD([sQuery(id+"F0.wireOp",EDGE,"E1"),sQuery(id+"F0.wireOp",EDGE,"E2"),sQuery(id+"F4.wireOp",EDGE,"E20.179.0"),sQuery(id+"F4.wireOp",EDGE,"E20.179.1")])]});
            var Q38;
            Q38=makeQuery(id+"F5.opExtrude","SWEPT_EDGE",EDGE,{"disambiguationData":[OSD([sQuery(id+"F4.wireOp",EDGE,"E20.178.1"),sQuery(id+"F4.wireOp",EDGE,"E20.179.0")])]});
            var Q39;
            Q39=makeQuery(id+"F5.opExtrude","SWEPT_EDGE",EDGE,{"disambiguationData":[OSD([sQuery(id+"F4.wireOp",EDGE,"E20.177.1"),sQuery(id+"F4.wireOp",EDGE,"E20.178.0")])]});
            var Q40;
            Q40=makeQuery(id+"F5.opExtrude","SWEPT_EDGE",EDGE,{"disambiguationData":[OSD([sQuery(id+"F4.wireOp",EDGE,"E20.176.1"),sQuery(id+"F4.wireOp",EDGE,"E20.177.0")])]});
            var Q41;
            Q41=makeQuery(id+"F5.opExtrude","SWEPT_EDGE",EDGE,{"disambiguationData":[OSD([sQuery(id+"F0.wireOp",EDGE,"E1"),sQuery(id+"F0.wireOp",EDGE,"E2"),sQuery(id+"F4.wireOp",EDGE,"E20.176.0"),sQuery(id+"F4.wireOp",EDGE,"E20.176.1")])]});
            var Q42;
            Q42=makeQuery(id+"F5.opExtrude","SWEPT_EDGE",EDGE,{"disambiguationData":[OSD([sQuery(id+"F4.wireOp",EDGE,"E20.175.1"),sQuery(id+"F4.wireOp",EDGE,"E20.176.0")])]});
            var Q43;
            Q43=makeQuery(id+"F5.opExtrude","SWEPT_EDGE",EDGE,{"disambiguationData":[OSD([sQuery(id+"F0.wireOp",EDGE,"E1"),sQuery(id+"F0.wireOp",EDGE,"E2"),sQuery(id+"F4.wireOp",EDGE,"E20.175.0"),sQuery(id+"F4.wireOp",EDGE,"E20.175.1")])]});
            var Q44;
            Q44=makeQuery(id+"F5.opExtrude","SWEPT_EDGE",EDGE,{"disambiguationData":[OSD([sQuery(id+"F4.wireOp",EDGE,"E20.174.1"),sQuery(id+"F4.wireOp",EDGE,"E20.175.0")])]});
            var Q45;
            Q45=makeQuery(id+"F5.opExtrude","SWEPT_EDGE",EDGE,{"disambiguationData":[OSD([sQuery(id+"F0.wireOp",EDGE,"E1"),sQuery(id+"F0.wireOp",EDGE,"E2"),sQuery(id+"F4.wireOp",EDGE,"E20.174.0"),sQuery(id+"F4.wireOp",EDGE,"E20.174.1")])]});
            var Q46;
            Q46=makeQuery(id+"F5.opExtrude","SWEPT_EDGE",EDGE,{"disambiguationData":[OSD([sQuery(id+"F4.wireOp",EDGE,"E20.173.1"),sQuery(id+"F4.wireOp",EDGE,"E20.174.0")])]});
            var Q47;
            Q47=makeQuery(id+"F5.opExtrude","SWEPT_EDGE",EDGE,{"disambiguationData":[OSD([sQuery(id+"F0.wireOp",EDGE,"E1"),sQuery(id+"F0.wireOp",EDGE,"E2"),sQuery(id+"F4.wireOp",EDGE,"E20.173.0"),sQuery(id+"F4.wireOp",EDGE,"E20.173.1")])]});
            var Q48;
            Q48=makeQuery(id+"F5.opExtrude","SWEPT_EDGE",EDGE,{"disambiguationData":[OSD([sQuery(id+"F4.wireOp",EDGE,"E20.172.1"),sQuery(id+"F4.wireOp",EDGE,"E20.173.0")])]});
            var Q49;
            Q49=makeQuery(id+"F5.opExtrude","SWEPT_EDGE",EDGE,{"disambiguationData":[OSD([sQuery(id+"F0.wireOp",EDGE,"E1"),sQuery(id+"F0.wireOp",EDGE,"E2"),sQuery(id+"F4.wireOp",EDGE,"E20.172.0"),sQuery(id+"F4.wireOp",EDGE,"E20.172.1")])]});
            var Q50;
            Q50=makeQuery(id+"F5.opExtrude","SWEPT_EDGE",EDGE,{"disambiguationData":[OSD([sQuery(id+"F4.wireOp",EDGE,"E20.171.1"),sQuery(id+"F4.wireOp",EDGE,"E20.172.0")])]});
            var Q51;
            Q51=makeQuery(id+"F5.opExtrude","SWEPT_EDGE",EDGE,{"disambiguationData":[OSD([sQuery(id+"F0.wireOp",EDGE,"E1"),sQuery(id+"F0.wireOp",EDGE,"E2"),sQuery(id+"F4.wireOp",EDGE,"E20.171.0"),sQuery(id+"F4.wireOp",EDGE,"E20.171.1")])]});
            var Q52;
            Q52=makeQuery(id+"F5.opExtrude","SWEPT_EDGE",EDGE,{"disambiguationData":[OSD([sQuery(id+"F4.wireOp",EDGE,"E20.170.1"),sQuery(id+"F4.wireOp",EDGE,"E20.171.0")])]});
            var Q53;
            Q53=makeQuery(id+"F5.opExtrude","SWEPT_EDGE",EDGE,{"disambiguationData":[OSD([sQuery(id+"F0.wireOp",EDGE,"E1"),sQuery(id+"F0.wireOp",EDGE,"E2"),sQuery(id+"F4.wireOp",EDGE,"E20.170.0"),sQuery(id+"F4.wireOp",EDGE,"E20.170.1")])]});
            var Q54;
            Q54=makeQuery(id+"F5.opExtrude","SWEPT_EDGE",EDGE,{"disambiguationData":[OSD([sQuery(id+"F4.wireOp",EDGE,"E20.169.1"),sQuery(id+"F4.wireOp",EDGE,"E20.170.0")])]});
            var Q55;
            Q55=makeQuery(id+"F5.opExtrude","SWEPT_EDGE",EDGE,{"disambiguationData":[OSD([sQuery(id+"F0.wireOp",EDGE,"E1"),sQuery(id+"F0.wireOp",EDGE,"E2"),sQuery(id+"F4.wireOp",EDGE,"E20.169.0"),sQuery(id+"F4.wireOp",EDGE,"E20.169.1")])]});
            var Q56;
            Q56=makeQuery(id+"F5.opExtrude","SWEPT_EDGE",EDGE,{"disambiguationData":[OSD([sQuery(id+"F4.wireOp",EDGE,"E20.168.1"),sQuery(id+"F4.wireOp",EDGE,"E20.169.0")])]});
            var Q57;
            Q57=makeQuery(id+"F5.opExtrude","SWEPT_EDGE",EDGE,{"disambiguationData":[OSD([sQuery(id+"F0.wireOp",EDGE,"E1"),sQuery(id+"F0.wireOp",EDGE,"E2"),sQuery(id+"F4.wireOp",EDGE,"E20.168.0"),sQuery(id+"F4.wireOp",EDGE,"E20.168.1")])]});
            var Q58;
            Q58=makeQuery(id+"F5.opExtrude","SWEPT_EDGE",EDGE,{"disambiguationData":[OSD([sQuery(id+"F4.wireOp",EDGE,"E20.167.1"),sQuery(id+"F4.wireOp",EDGE,"E20.168.0")])]});
            var Q59;
            Q59=makeQuery(id+"F5.opExtrude","SWEPT_EDGE",EDGE,{"disambiguationData":[OSD([sQuery(id+"F0.wireOp",EDGE,"E1"),sQuery(id+"F0.wireOp",EDGE,"E2"),sQuery(id+"F4.wireOp",EDGE,"E20.167.0"),sQuery(id+"F4.wireOp",EDGE,"E20.167.1")])]});
            var Q60;
            Q60=makeQuery(id+"F5.opExtrude","SWEPT_EDGE",EDGE,{"disambiguationData":[OSD([sQuery(id+"F4.wireOp",EDGE,"E20.166.1"),sQuery(id+"F4.wireOp",EDGE,"E20.167.0")])]});
            var Q61;
            Q61=makeQuery(id+"F5.opExtrude","SWEPT_EDGE",EDGE,{"disambiguationData":[OSD([sQuery(id+"F0.wireOp",EDGE,"E1"),sQuery(id+"F0.wireOp",EDGE,"E2"),sQuery(id+"F4.wireOp",EDGE,"E20.166.0"),sQuery(id+"F4.wireOp",EDGE,"E20.166.1")])]});
            var Q62;
            Q62=makeQuery(id+"F5.opExtrude","SWEPT_EDGE",EDGE,{"disambiguationData":[OSD([sQuery(id+"F4.wireOp",EDGE,"E20.165.1"),sQuery(id+"F4.wireOp",EDGE,"E20.166.0")])]});
            var Q63;
            Q63=makeQuery(id+"F5.opExtrude","SWEPT_EDGE",EDGE,{"disambiguationData":[OSD([sQuery(id+"F0.wireOp",EDGE,"E1"),sQuery(id+"F0.wireOp",EDGE,"E2"),sQuery(id+"F4.wireOp",EDGE,"E20.165.0"),sQuery(id+"F4.wireOp",EDGE,"E20.165.1")])]});
            var Q64;
            Q64=makeQuery(id+"F5.opExtrude","SWEPT_EDGE",EDGE,{"disambiguationData":[OSD([sQuery(id+"F4.wireOp",EDGE,"E20.164.1"),sQuery(id+"F4.wireOp",EDGE,"E20.165.0")])]});
            var Q65;
            Q65=makeQuery(id+"F5.opExtrude","SWEPT_EDGE",EDGE,{"disambiguationData":[OSD([sQuery(id+"F0.wireOp",EDGE,"E1"),sQuery(id+"F0.wireOp",EDGE,"E2"),sQuery(id+"F4.wireOp",EDGE,"E20.164.0"),sQuery(id+"F4.wireOp",EDGE,"E20.164.1")])]});
            var Q66;
            Q66=makeQuery(id+"F5.opExtrude","SWEPT_EDGE",EDGE,{"disambiguationData":[OSD([sQuery(id+"F4.wireOp",EDGE,"E20.163.1"),sQuery(id+"F4.wireOp",EDGE,"E20.164.0")])]});
            var Q67;
            Q67=makeQuery(id+"F5.opExtrude","SWEPT_EDGE",EDGE,{"disambiguationData":[OSD([sQuery(id+"F0.wireOp",EDGE,"E1"),sQuery(id+"F0.wireOp",EDGE,"E2"),sQuery(id+"F4.wireOp",EDGE,"E20.163.0"),sQuery(id+"F4.wireOp",EDGE,"E20.163.1")])]});
            var Q68;
            Q68=makeQuery(id+"F5.opExtrude","SWEPT_EDGE",EDGE,{"disambiguationData":[OSD([sQuery(id+"F4.wireOp",EDGE,"E20.162.1"),sQuery(id+"F4.wireOp",EDGE,"E20.163.0")])]});
            var Q69;
            Q69=makeQuery(id+"F5.opExtrude","SWEPT_EDGE",EDGE,{"disambiguationData":[OSD([sQuery(id+"F0.wireOp",EDGE,"E1"),sQuery(id+"F0.wireOp",EDGE,"E2"),sQuery(id+"F4.wireOp",EDGE,"E20.162.0"),sQuery(id+"F4.wireOp",EDGE,"E20.162.1")])]});
            var Q70;
            Q70=makeQuery(id+"F5.opExtrude","SWEPT_EDGE",EDGE,{"disambiguationData":[OSD([sQuery(id+"F4.wireOp",EDGE,"E20.161.1"),sQuery(id+"F4.wireOp",EDGE,"E20.162.0")])]});
            var Q71;
            Q71=makeQuery(id+"F5.opExtrude","SWEPT_EDGE",EDGE,{"disambiguationData":[OSD([sQuery(id+"F0.wireOp",EDGE,"E1"),sQuery(id+"F0.wireOp",EDGE,"E2"),sQuery(id+"F4.wireOp",EDGE,"E20.161.0"),sQuery(id+"F4.wireOp",EDGE,"E20.161.1")])]});
            var Q72;
            Q72=makeQuery(id+"F5.opExtrude","SWEPT_EDGE",EDGE,{"disambiguationData":[OSD([sQuery(id+"F4.wireOp",EDGE,"E20.160.1"),sQuery(id+"F4.wireOp",EDGE,"E20.161.0")])]});
            var Q73;
            Q73=makeQuery(id+"F5.opExtrude","SWEPT_EDGE",EDGE,{"disambiguationData":[OSD([sQuery(id+"F0.wireOp",EDGE,"E1"),sQuery(id+"F0.wireOp",EDGE,"E2"),sQuery(id+"F4.wireOp",EDGE,"E20.160.0"),sQuery(id+"F4.wireOp",EDGE,"E20.160.1")])]});
            var Q74;
            Q74=makeQuery(id+"F5.opExtrude","SWEPT_EDGE",EDGE,{"disambiguationData":[OSD([sQuery(id+"F4.wireOp",EDGE,"E20.159.1"),sQuery(id+"F4.wireOp",EDGE,"E20.160.0")])]});
            var Q75;
            Q75=makeQuery(id+"F5.opExtrude","SWEPT_EDGE",EDGE,{"disambiguationData":[OSD([sQuery(id+"F0.wireOp",EDGE,"E1"),sQuery(id+"F0.wireOp",EDGE,"E2"),sQuery(id+"F4.wireOp",EDGE,"E20.159.0"),sQuery(id+"F4.wireOp",EDGE,"E20.159.1")])]});
            var Q76;
            Q76=makeQuery(id+"F5.opExtrude","SWEPT_EDGE",EDGE,{"disambiguationData":[OSD([sQuery(id+"F4.wireOp",EDGE,"E20.158.1"),sQuery(id+"F4.wireOp",EDGE,"E20.159.0")])]});
            var Q77;
            Q77=makeQuery(id+"F5.opExtrude","SWEPT_EDGE",EDGE,{"disambiguationData":[OSD([sQuery(id+"F0.wireOp",EDGE,"E1"),sQuery(id+"F0.wireOp",EDGE,"E2"),sQuery(id+"F4.wireOp",EDGE,"E20.158.0"),sQuery(id+"F4.wireOp",EDGE,"E20.158.1")])]});
            var Q78;
            Q78=makeQuery(id+"F5.opExtrude","SWEPT_EDGE",EDGE,{"disambiguationData":[OSD([sQuery(id+"F4.wireOp",EDGE,"E20.157.1"),sQuery(id+"F4.wireOp",EDGE,"E20.158.0")])]});
            var Q79;
            Q79=makeQuery(id+"F5.opExtrude","SWEPT_EDGE",EDGE,{"disambiguationData":[OSD([sQuery(id+"F0.wireOp",EDGE,"E1"),sQuery(id+"F0.wireOp",EDGE,"E2"),sQuery(id+"F4.wireOp",EDGE,"E20.157.0"),sQuery(id+"F4.wireOp",EDGE,"E20.157.1")])]});
            var Q80;
            Q80=makeQuery(id+"F5.opExtrude","SWEPT_EDGE",EDGE,{"disambiguationData":[OSD([sQuery(id+"F4.wireOp",EDGE,"E20.156.1"),sQuery(id+"F4.wireOp",EDGE,"E20.157.0")])]});
            var Q81;
            Q81=makeQuery(id+"F5.opExtrude","SWEPT_EDGE",EDGE,{"disambiguationData":[OSD([sQuery(id+"F0.wireOp",EDGE,"E1"),sQuery(id+"F0.wireOp",EDGE,"E2"),sQuery(id+"F4.wireOp",EDGE,"E20.156.0"),sQuery(id+"F4.wireOp",EDGE,"E20.156.1")])]});
            var Q82;
            Q82=makeQuery(id+"F5.opExtrude","SWEPT_EDGE",EDGE,{"disambiguationData":[OSD([sQuery(id+"F4.wireOp",EDGE,"E20.155.1"),sQuery(id+"F4.wireOp",EDGE,"E20.156.0")])]});
            var Q83;
            Q83=makeQuery(id+"F5.opExtrude","SWEPT_EDGE",EDGE,{"disambiguationData":[OSD([sQuery(id+"F0.wireOp",EDGE,"E1"),sQuery(id+"F0.wireOp",EDGE,"E2"),sQuery(id+"F4.wireOp",EDGE,"E20.155.0"),sQuery(id+"F4.wireOp",EDGE,"E20.155.1")])]});
            var Q84;
            Q84=makeQuery(id+"F5.opExtrude","SWEPT_EDGE",EDGE,{"disambiguationData":[OSD([sQuery(id+"F4.wireOp",EDGE,"E20.154.1"),sQuery(id+"F4.wireOp",EDGE,"E20.155.0")])]});
            var Q85;
            Q85=makeQuery(id+"F5.opExtrude","SWEPT_EDGE",EDGE,{"disambiguationData":[OSD([sQuery(id+"F0.wireOp",EDGE,"E1"),sQuery(id+"F0.wireOp",EDGE,"E2"),sQuery(id+"F4.wireOp",EDGE,"E20.154.0"),sQuery(id+"F4.wireOp",EDGE,"E20.154.1")])]});
            var Q86;
            Q86=makeQuery(id+"F5.opExtrude","SWEPT_EDGE",EDGE,{"disambiguationData":[OSD([sQuery(id+"F4.wireOp",EDGE,"E20.153.1"),sQuery(id+"F4.wireOp",EDGE,"E20.154.0")])]});
            var Q87;
            Q87=makeQuery(id+"F5.opExtrude","SWEPT_EDGE",EDGE,{"disambiguationData":[OSD([sQuery(id+"F0.wireOp",EDGE,"E1"),sQuery(id+"F0.wireOp",EDGE,"E2"),sQuery(id+"F4.wireOp",EDGE,"E20.153.0"),sQuery(id+"F4.wireOp",EDGE,"E20.153.1")])]});
            var Q88;
            Q88=makeQuery(id+"F5.opExtrude","SWEPT_EDGE",EDGE,{"disambiguationData":[OSD([sQuery(id+"F4.wireOp",EDGE,"E20.152.1"),sQuery(id+"F4.wireOp",EDGE,"E20.153.0")])]});
            var Q89;
            Q89=makeQuery(id+"F5.opExtrude","SWEPT_EDGE",EDGE,{"disambiguationData":[OSD([sQuery(id+"F0.wireOp",EDGE,"E1"),sQuery(id+"F0.wireOp",EDGE,"E2"),sQuery(id+"F4.wireOp",EDGE,"E20.152.0"),sQuery(id+"F4.wireOp",EDGE,"E20.152.1")])]});
            var Q90;
            Q90=makeQuery(id+"F5.opExtrude","SWEPT_EDGE",EDGE,{"disambiguationData":[OSD([sQuery(id+"F4.wireOp",EDGE,"E20.151.1"),sQuery(id+"F4.wireOp",EDGE,"E20.152.0")])]});
            var Q91;
            Q91=makeQuery(id+"F5.opExtrude","SWEPT_EDGE",EDGE,{"disambiguationData":[OSD([sQuery(id+"F0.wireOp",EDGE,"E1"),sQuery(id+"F0.wireOp",EDGE,"E2"),sQuery(id+"F4.wireOp",EDGE,"E20.151.0"),sQuery(id+"F4.wireOp",EDGE,"E20.151.1")])]});
            var Q92;
            Q92=makeQuery(id+"F5.opExtrude","SWEPT_EDGE",EDGE,{"disambiguationData":[OSD([sQuery(id+"F4.wireOp",EDGE,"E20.150.1"),sQuery(id+"F4.wireOp",EDGE,"E20.151.0")])]});
            var Q93;
            Q93=makeQuery(id+"F5.opExtrude","SWEPT_EDGE",EDGE,{"disambiguationData":[OSD([sQuery(id+"F0.wireOp",EDGE,"E1"),sQuery(id+"F0.wireOp",EDGE,"E2"),sQuery(id+"F4.wireOp",EDGE,"E20.150.0"),sQuery(id+"F4.wireOp",EDGE,"E20.150.1")])]});
            var Q94;
            Q94=makeQuery(id+"F5.opExtrude","SWEPT_EDGE",EDGE,{"disambiguationData":[OSD([sQuery(id+"F4.wireOp",EDGE,"E20.149.1"),sQuery(id+"F4.wireOp",EDGE,"E20.150.0")])]});
            var Q95;
            Q95=makeQuery(id+"F5.opExtrude","SWEPT_EDGE",EDGE,{"disambiguationData":[OSD([sQuery(id+"F0.wireOp",EDGE,"E1"),sQuery(id+"F0.wireOp",EDGE,"E2"),sQuery(id+"F4.wireOp",EDGE,"E20.149.0"),sQuery(id+"F4.wireOp",EDGE,"E20.149.1")])]});
            var Q96;
            Q96=makeQuery(id+"F5.opExtrude","SWEPT_EDGE",EDGE,{"disambiguationData":[OSD([sQuery(id+"F4.wireOp",EDGE,"E20.148.1"),sQuery(id+"F4.wireOp",EDGE,"E20.149.0")])]});
            var Q97;
            Q97=makeQuery(id+"F5.opExtrude","SWEPT_EDGE",EDGE,{"disambiguationData":[OSD([sQuery(id+"F0.wireOp",EDGE,"E1"),sQuery(id+"F0.wireOp",EDGE,"E2"),sQuery(id+"F4.wireOp",EDGE,"E20.148.0"),sQuery(id+"F4.wireOp",EDGE,"E20.148.1")])]});
            var Q98;
            Q98=makeQuery(id+"F5.opExtrude","SWEPT_EDGE",EDGE,{"disambiguationData":[OSD([sQuery(id+"F4.wireOp",EDGE,"E20.147.1"),sQuery(id+"F4.wireOp",EDGE,"E20.148.0")])]});
            var Q99;
            Q99=makeQuery(id+"F5.opExtrude","SWEPT_EDGE",EDGE,{"disambiguationData":[OSD([sQuery(id+"F0.wireOp",EDGE,"E1"),sQuery(id+"F0.wireOp",EDGE,"E2"),sQuery(id+"F4.wireOp",EDGE,"E20.147.0"),sQuery(id+"F4.wireOp",EDGE,"E20.147.1")])]});
            var Q100;
            Q100=makeQuery(id+"F5.opExtrude","SWEPT_EDGE",EDGE,{"disambiguationData":[OSD([sQuery(id+"F4.wireOp",EDGE,"E20.146.1"),sQuery(id+"F4.wireOp",EDGE,"E20.147.0")])]});
            var Q101;
            Q101=makeQuery(id+"F5.opExtrude","SWEPT_EDGE",EDGE,{"disambiguationData":[OSD([sQuery(id+"F0.wireOp",EDGE,"E1"),sQuery(id+"F0.wireOp",EDGE,"E2"),sQuery(id+"F4.wireOp",EDGE,"E20.146.0"),sQuery(id+"F4.wireOp",EDGE,"E20.146.1")])]});
            var Q102;
            Q102=makeQuery(id+"F5.opExtrude","SWEPT_EDGE",EDGE,{"disambiguationData":[OSD([sQuery(id+"F4.wireOp",EDGE,"E20.145.1"),sQuery(id+"F4.wireOp",EDGE,"E20.146.0")])]});
            var Q103;
            Q103=makeQuery(id+"F5.opExtrude","SWEPT_EDGE",EDGE,{"disambiguationData":[OSD([sQuery(id+"F0.wireOp",EDGE,"E1"),sQuery(id+"F0.wireOp",EDGE,"E2"),sQuery(id+"F4.wireOp",EDGE,"E20.145.0"),sQuery(id+"F4.wireOp",EDGE,"E20.145.1")])]});
            var Q104;
            Q104=makeQuery(id+"F5.opExtrude","SWEPT_EDGE",EDGE,{"disambiguationData":[OSD([sQuery(id+"F4.wireOp",EDGE,"E20.144.1"),sQuery(id+"F4.wireOp",EDGE,"E20.145.0")])]});
            var Q105;
            Q105=makeQuery(id+"F5.opExtrude","SWEPT_EDGE",EDGE,{"disambiguationData":[OSD([sQuery(id+"F0.wireOp",EDGE,"E1"),sQuery(id+"F0.wireOp",EDGE,"E2"),sQuery(id+"F4.wireOp",EDGE,"E20.144.0"),sQuery(id+"F4.wireOp",EDGE,"E20.144.1")])]});
            var Q106;
            Q106=makeQuery(id+"F5.opExtrude","SWEPT_EDGE",EDGE,{"disambiguationData":[OSD([sQuery(id+"F4.wireOp",EDGE,"E20.143.1"),sQuery(id+"F4.wireOp",EDGE,"E20.144.0")])]});
            var Q107;
            Q107=makeQuery(id+"F5.opExtrude","SWEPT_EDGE",EDGE,{"disambiguationData":[OSD([sQuery(id+"F0.wireOp",EDGE,"E1"),sQuery(id+"F0.wireOp",EDGE,"E2"),sQuery(id+"F4.wireOp",EDGE,"E20.143.0"),sQuery(id+"F4.wireOp",EDGE,"E20.143.1")])]});
            var Q108;
            Q108=makeQuery(id+"F5.opExtrude","SWEPT_EDGE",EDGE,{"disambiguationData":[OSD([sQuery(id+"F4.wireOp",EDGE,"E20.142.1"),sQuery(id+"F4.wireOp",EDGE,"E20.143.0")])]});
            var Q109;
            Q109=makeQuery(id+"F5.opExtrude","SWEPT_EDGE",EDGE,{"disambiguationData":[OSD([sQuery(id+"F0.wireOp",EDGE,"E1"),sQuery(id+"F0.wireOp",EDGE,"E2"),sQuery(id+"F4.wireOp",EDGE,"E20.142.0"),sQuery(id+"F4.wireOp",EDGE,"E20.142.1")])]});
            var Q110;
            Q110=makeQuery(id+"F5.opExtrude","SWEPT_EDGE",EDGE,{"disambiguationData":[OSD([sQuery(id+"F4.wireOp",EDGE,"E20.141.1"),sQuery(id+"F4.wireOp",EDGE,"E20.142.0")])]});
            var Q111;
            Q111=makeQuery(id+"F5.opExtrude","SWEPT_EDGE",EDGE,{"disambiguationData":[OSD([sQuery(id+"F0.wireOp",EDGE,"E1"),sQuery(id+"F0.wireOp",EDGE,"E2"),sQuery(id+"F4.wireOp",EDGE,"E20.141.0"),sQuery(id+"F4.wireOp",EDGE,"E20.141.1")])]});
            var Q112;
            Q112=makeQuery(id+"F5.opExtrude","SWEPT_EDGE",EDGE,{"disambiguationData":[OSD([sQuery(id+"F4.wireOp",EDGE,"E20.140.1"),sQuery(id+"F4.wireOp",EDGE,"E20.141.0")])]});
            var Q113;
            Q113=makeQuery(id+"F5.opExtrude","SWEPT_EDGE",EDGE,{"disambiguationData":[OSD([sQuery(id+"F0.wireOp",EDGE,"E1"),sQuery(id+"F0.wireOp",EDGE,"E2"),sQuery(id+"F4.wireOp",EDGE,"E20.140.0"),sQuery(id+"F4.wireOp",EDGE,"E20.140.1")])]});
            var Q114;
            Q114=makeQuery(id+"F5.opExtrude","SWEPT_EDGE",EDGE,{"disambiguationData":[OSD([sQuery(id+"F4.wireOp",EDGE,"E20.139.1"),sQuery(id+"F4.wireOp",EDGE,"E20.140.0")])]});
            var Q115;
            Q115=makeQuery(id+"F5.opExtrude","SWEPT_EDGE",EDGE,{"disambiguationData":[OSD([sQuery(id+"F0.wireOp",EDGE,"E1"),sQuery(id+"F0.wireOp",EDGE,"E2"),sQuery(id+"F4.wireOp",EDGE,"E20.139.0"),sQuery(id+"F4.wireOp",EDGE,"E20.139.1")])]});
            var Q116;
            Q116=makeQuery(id+"F5.opExtrude","SWEPT_EDGE",EDGE,{"disambiguationData":[OSD([sQuery(id+"F4.wireOp",EDGE,"E20.138.1"),sQuery(id+"F4.wireOp",EDGE,"E20.139.0")])]});
            var Q117;
            Q117=makeQuery(id+"F5.opExtrude","SWEPT_EDGE",EDGE,{"disambiguationData":[OSD([sQuery(id+"F0.wireOp",EDGE,"E1"),sQuery(id+"F0.wireOp",EDGE,"E2"),sQuery(id+"F4.wireOp",EDGE,"E20.138.0"),sQuery(id+"F4.wireOp",EDGE,"E20.138.1")])]});
            var Q118;
            Q118=makeQuery(id+"F5.opExtrude","SWEPT_EDGE",EDGE,{"disambiguationData":[OSD([sQuery(id+"F4.wireOp",EDGE,"E20.137.1"),sQuery(id+"F4.wireOp",EDGE,"E20.138.0")])]});
            var Q119;
            Q119=makeQuery(id+"F5.opExtrude","SWEPT_EDGE",EDGE,{"disambiguationData":[OSD([sQuery(id+"F0.wireOp",EDGE,"E1"),sQuery(id+"F0.wireOp",EDGE,"E2"),sQuery(id+"F4.wireOp",EDGE,"E20.137.0"),sQuery(id+"F4.wireOp",EDGE,"E20.137.1")])]});
            var Q120;
            Q120=makeQuery(id+"F5.opExtrude","SWEPT_EDGE",EDGE,{"disambiguationData":[OSD([sQuery(id+"F4.wireOp",EDGE,"E20.136.1"),sQuery(id+"F4.wireOp",EDGE,"E20.137.0")])]});
            var Q121;
            Q121=makeQuery(id+"F5.opExtrude","SWEPT_EDGE",EDGE,{"disambiguationData":[OSD([sQuery(id+"F0.wireOp",EDGE,"E1"),sQuery(id+"F0.wireOp",EDGE,"E2"),sQuery(id+"F4.wireOp",EDGE,"E20.136.0"),sQuery(id+"F4.wireOp",EDGE,"E20.136.1")])]});
            var Q122;
            Q122=makeQuery(id+"F5.opExtrude","SWEPT_EDGE",EDGE,{"disambiguationData":[OSD([sQuery(id+"F4.wireOp",EDGE,"E20.135.1"),sQuery(id+"F4.wireOp",EDGE,"E20.136.0")])]});
            var Q123;
            Q123=makeQuery(id+"F5.opExtrude","SWEPT_EDGE",EDGE,{"disambiguationData":[OSD([sQuery(id+"F0.wireOp",EDGE,"E1"),sQuery(id+"F0.wireOp",EDGE,"E2"),sQuery(id+"F4.wireOp",EDGE,"E20.135.0"),sQuery(id+"F4.wireOp",EDGE,"E20.135.1")])]});
            var Q124;
            Q124=makeQuery(id+"F5.opExtrude","SWEPT_EDGE",EDGE,{"disambiguationData":[OSD([sQuery(id+"F4.wireOp",EDGE,"E20.134.1"),sQuery(id+"F4.wireOp",EDGE,"E20.135.0")])]});
            var Q125;
            Q125=makeQuery(id+"F5.opExtrude","SWEPT_EDGE",EDGE,{"disambiguationData":[OSD([sQuery(id+"F0.wireOp",EDGE,"E1"),sQuery(id+"F0.wireOp",EDGE,"E2"),sQuery(id+"F4.wireOp",EDGE,"E20.134.0"),sQuery(id+"F4.wireOp",EDGE,"E20.134.1")])]});
            var Q126;
            Q126=makeQuery(id+"F5.opExtrude","SWEPT_EDGE",EDGE,{"disambiguationData":[OSD([sQuery(id+"F0.wireOp",EDGE,"E1"),sQuery(id+"F0.wireOp",EDGE,"E2"),sQuery(id+"F4.wireOp",EDGE,"E20.133.0"),sQuery(id+"F4.wireOp",EDGE,"E20.133.1")])]});
            var Q127;
            Q127=makeQuery(id+"F5.opExtrude","SWEPT_EDGE",EDGE,{"disambiguationData":[OSD([sQuery(id+"F4.wireOp",EDGE,"E20.133.1"),sQuery(id+"F4.wireOp",EDGE,"E20.134.0")])]});
            var Q128;
            Q128=makeQuery(id+"F5.opExtrude","SWEPT_EDGE",EDGE,{"disambiguationData":[OSD([sQuery(id+"F4.wireOp",EDGE,"E20.132.1"),sQuery(id+"F4.wireOp",EDGE,"E20.133.0")])]});
            var Q129;
            Q129=makeQuery(id+"F5.opExtrude","SWEPT_EDGE",EDGE,{"disambiguationData":[OSD([sQuery(id+"F0.wireOp",EDGE,"E1"),sQuery(id+"F0.wireOp",EDGE,"E2"),sQuery(id+"F4.wireOp",EDGE,"E20.132.0"),sQuery(id+"F4.wireOp",EDGE,"E20.132.1")])]});
            var Q130;
            Q130=makeQuery(id+"F5.opExtrude","SWEPT_EDGE",EDGE,{"disambiguationData":[OSD([sQuery(id+"F4.wireOp",EDGE,"E20.131.1"),sQuery(id+"F4.wireOp",EDGE,"E20.132.0")])]});
            var Q131;
            Q131=makeQuery(id+"F5.opExtrude","SWEPT_EDGE",EDGE,{"disambiguationData":[OSD([sQuery(id+"F0.wireOp",EDGE,"E1"),sQuery(id+"F0.wireOp",EDGE,"E2"),sQuery(id+"F4.wireOp",EDGE,"E20.131.0"),sQuery(id+"F4.wireOp",EDGE,"E20.131.1")])]});
            var Q132;
            Q132=makeQuery(id+"F5.opExtrude","SWEPT_EDGE",EDGE,{"disambiguationData":[OSD([sQuery(id+"F4.wireOp",EDGE,"E20.130.1"),sQuery(id+"F4.wireOp",EDGE,"E20.131.0")])]});
            var Q133;
            Q133=makeQuery(id+"F5.opExtrude","SWEPT_EDGE",EDGE,{"disambiguationData":[OSD([sQuery(id+"F0.wireOp",EDGE,"E1"),sQuery(id+"F0.wireOp",EDGE,"E2"),sQuery(id+"F4.wireOp",EDGE,"E20.130.0"),sQuery(id+"F4.wireOp",EDGE,"E20.130.1")])]});
            fillet(context, id + "F7", {"entities" : qUnion([Q0, Q1, Q2, Q3, Q4, Q5, Q6, Q7, Q8, Q9, Q10, Q11, Q12, Q13, Q14, Q15, Q16, Q17, Q18, Q19, Q20, Q21, Q22, Q23, Q24, Q25, Q26, Q27, Q28, Q29, Q30, Q31, Q32, Q33, Q34, Q35, Q36, Q37, Q38, Q39, Q40, Q41, Q42, Q43, Q44, Q45, Q46, Q47, Q48, Q49, Q50, Q51, Q52, Q53, Q54, Q55, Q56, Q57, Q58, Q59, Q60, Q61, Q62, Q63, Q64, Q65, Q66, Q67, Q68, Q69, Q70, Q71, Q72, Q73, Q74, Q75, Q76, Q77, Q78, Q79, Q80, Q81, Q82, Q83, Q84, Q85, Q86, Q87, Q88, Q89, Q90, Q91, Q92, Q93, Q94, Q95, Q96, Q97, Q98, Q99, Q100, Q101, Q102, Q103, Q104, Q105, Q106, Q107, Q108, Q109, Q110, Q111, Q112, Q113, Q114, Q115, Q116, Q117, Q118, Q119, Q120, Q121, Q122, Q123, Q124, Q125, Q126, Q127, Q128, Q129, Q130, Q131, Q132, Q133]), "radius" : .2 * mm, "tangentPropagation" : true, "allowEdgeOverflow" : false});
        }
        {
            var Q0;
            Q0 = qSketchRegion(id + "F2", true);
            extrude(context, id + "F8", {"entities" : qUnion([Q0]), "operationType" : NewBodyOperationType.REMOVE, "endBound" : BoundingType.UP_TO_NEXT, "oppositeDirection" : true, "depth" : 25 * mm});
        }
        {
            var Q0;
            Q0=makeQuery(id+"F5.opExtrude","SWEPT_EDGE",EDGE,{"disambiguationData":[OSD([sQuery(id+"F4.wireOp",EDGE,"E20.129.1"),sQuery(id+"F4.wireOp",EDGE,"E20.130.0")])]});
            var Q1;
            Q1=makeQuery(id+"F5.opExtrude","SWEPT_EDGE",EDGE,{"disambiguationData":[OSD([sQuery(id+"F0.wireOp",EDGE,"E1"),sQuery(id+"F0.wireOp",EDGE,"E2"),sQuery(id+"F4.wireOp",EDGE,"E20.129.0"),sQuery(id+"F4.wireOp",EDGE,"E20.129.1")])]});
            var Q2;
            Q2=makeQuery(id+"F5.opExtrude","SWEPT_EDGE",EDGE,{"disambiguationData":[OSD([sQuery(id+"F4.wireOp",EDGE,"E20.128.1"),sQuery(id+"F4.wireOp",EDGE,"E20.129.0")])]});
            var Q3;
            Q3=makeQuery(id+"F5.opExtrude","SWEPT_EDGE",EDGE,{"disambiguationData":[OSD([sQuery(id+"F0.wireOp",EDGE,"E1"),sQuery(id+"F0.wireOp",EDGE,"E2"),sQuery(id+"F4.wireOp",EDGE,"E20.128.0"),sQuery(id+"F4.wireOp",EDGE,"E20.128.1")])]});
            var Q4;
            Q4=makeQuery(id+"F5.opExtrude","SWEPT_EDGE",EDGE,{"disambiguationData":[OSD([sQuery(id+"F4.wireOp",EDGE,"E20.127.1"),sQuery(id+"F4.wireOp",EDGE,"E20.128.0")])]});
            var Q5;
            Q5=makeQuery(id+"F5.opExtrude","SWEPT_EDGE",EDGE,{"disambiguationData":[OSD([sQuery(id+"F0.wireOp",EDGE,"E1"),sQuery(id+"F0.wireOp",EDGE,"E2"),sQuery(id+"F4.wireOp",EDGE,"E20.127.0"),sQuery(id+"F4.wireOp",EDGE,"E20.127.1")])]});
            var Q6;
            Q6=makeQuery(id+"F5.opExtrude","SWEPT_EDGE",EDGE,{"disambiguationData":[OSD([sQuery(id+"F4.wireOp",EDGE,"E20.126.1"),sQuery(id+"F4.wireOp",EDGE,"E20.127.0")])]});
            var Q7;
            Q7=makeQuery(id+"F5.opExtrude","SWEPT_EDGE",EDGE,{"disambiguationData":[OSD([sQuery(id+"F0.wireOp",EDGE,"E1"),sQuery(id+"F0.wireOp",EDGE,"E2"),sQuery(id+"F4.wireOp",EDGE,"E20.126.0"),sQuery(id+"F4.wireOp",EDGE,"E20.126.1")])]});
            var Q8;
            Q8=makeQuery(id+"F5.opExtrude","SWEPT_EDGE",EDGE,{"disambiguationData":[OSD([sQuery(id+"F4.wireOp",EDGE,"E20.125.1"),sQuery(id+"F4.wireOp",EDGE,"E20.126.0")])]});
            var Q9;
            Q9=makeQuery(id+"F5.opExtrude","SWEPT_EDGE",EDGE,{"disambiguationData":[OSD([sQuery(id+"F0.wireOp",EDGE,"E1"),sQuery(id+"F0.wireOp",EDGE,"E2"),sQuery(id+"F4.wireOp",EDGE,"E20.125.0"),sQuery(id+"F4.wireOp",EDGE,"E20.125.1")])]});
            var Q10;
            Q10=makeQuery(id+"F5.opExtrude","SWEPT_EDGE",EDGE,{"disambiguationData":[OSD([sQuery(id+"F4.wireOp",EDGE,"E20.124.1"),sQuery(id+"F4.wireOp",EDGE,"E20.125.0")])]});
            var Q11;
            Q11=makeQuery(id+"F5.opExtrude","SWEPT_EDGE",EDGE,{"disambiguationData":[OSD([sQuery(id+"F0.wireOp",EDGE,"E1"),sQuery(id+"F0.wireOp",EDGE,"E2"),sQuery(id+"F4.wireOp",EDGE,"E20.124.0"),sQuery(id+"F4.wireOp",EDGE,"E20.124.1")])]});
            var Q12;
            Q12=makeQuery(id+"F5.opExtrude","SWEPT_EDGE",EDGE,{"disambiguationData":[OSD([sQuery(id+"F4.wireOp",EDGE,"E20.123.1"),sQuery(id+"F4.wireOp",EDGE,"E20.124.0")])]});
            var Q13;
            Q13=makeQuery(id+"F5.opExtrude","SWEPT_EDGE",EDGE,{"disambiguationData":[OSD([sQuery(id+"F0.wireOp",EDGE,"E1"),sQuery(id+"F0.wireOp",EDGE,"E2"),sQuery(id+"F4.wireOp",EDGE,"E20.123.0"),sQuery(id+"F4.wireOp",EDGE,"E20.123.1")])]});
            var Q14;
            Q14=makeQuery(id+"F5.opExtrude","SWEPT_EDGE",EDGE,{"disambiguationData":[OSD([sQuery(id+"F4.wireOp",EDGE,"E20.122.1"),sQuery(id+"F4.wireOp",EDGE,"E20.123.0")])]});
            var Q15;
            Q15=makeQuery(id+"F5.opExtrude","SWEPT_EDGE",EDGE,{"disambiguationData":[OSD([sQuery(id+"F0.wireOp",EDGE,"E1"),sQuery(id+"F0.wireOp",EDGE,"E2"),sQuery(id+"F4.wireOp",EDGE,"E20.122.0"),sQuery(id+"F4.wireOp",EDGE,"E20.122.1")])]});
            var Q16;
            Q16=makeQuery(id+"F5.opExtrude","SWEPT_EDGE",EDGE,{"disambiguationData":[OSD([sQuery(id+"F4.wireOp",EDGE,"E20.121.1"),sQuery(id+"F4.wireOp",EDGE,"E20.122.0")])]});
            var Q17;
            Q17=makeQuery(id+"F5.opExtrude","SWEPT_EDGE",EDGE,{"disambiguationData":[OSD([sQuery(id+"F0.wireOp",EDGE,"E1"),sQuery(id+"F0.wireOp",EDGE,"E2"),sQuery(id+"F4.wireOp",EDGE,"E20.121.0"),sQuery(id+"F4.wireOp",EDGE,"E20.121.1")])]});
            var Q18;
            Q18=makeQuery(id+"F5.opExtrude","SWEPT_EDGE",EDGE,{"disambiguationData":[OSD([sQuery(id+"F4.wireOp",EDGE,"E20.120.1"),sQuery(id+"F4.wireOp",EDGE,"E20.121.0")])]});
            var Q19;
            Q19=makeQuery(id+"F5.opExtrude","SWEPT_EDGE",EDGE,{"disambiguationData":[OSD([sQuery(id+"F0.wireOp",EDGE,"E1"),sQuery(id+"F0.wireOp",EDGE,"E2"),sQuery(id+"F4.wireOp",EDGE,"E20.120.0"),sQuery(id+"F4.wireOp",EDGE,"E20.120.1")])]});
            var Q20;
            Q20=makeQuery(id+"F5.opExtrude","SWEPT_EDGE",EDGE,{"disambiguationData":[OSD([sQuery(id+"F4.wireOp",EDGE,"E20.119.1"),sQuery(id+"F4.wireOp",EDGE,"E20.120.0")])]});
            var Q21;
            Q21=makeQuery(id+"F5.opExtrude","SWEPT_EDGE",EDGE,{"disambiguationData":[OSD([sQuery(id+"F0.wireOp",EDGE,"E1"),sQuery(id+"F0.wireOp",EDGE,"E2"),sQuery(id+"F4.wireOp",EDGE,"E20.119.0"),sQuery(id+"F4.wireOp",EDGE,"E20.119.1")])]});
            var Q22;
            Q22=makeQuery(id+"F5.opExtrude","SWEPT_EDGE",EDGE,{"disambiguationData":[OSD([sQuery(id+"F4.wireOp",EDGE,"E20.118.1"),sQuery(id+"F4.wireOp",EDGE,"E20.119.0")])]});
            var Q23;
            Q23=makeQuery(id+"F5.opExtrude","SWEPT_EDGE",EDGE,{"disambiguationData":[OSD([sQuery(id+"F0.wireOp",EDGE,"E1"),sQuery(id+"F0.wireOp",EDGE,"E2"),sQuery(id+"F4.wireOp",EDGE,"E20.118.0"),sQuery(id+"F4.wireOp",EDGE,"E20.118.1")])]});
            var Q24;
            Q24=makeQuery(id+"F5.opExtrude","SWEPT_EDGE",EDGE,{"disambiguationData":[OSD([sQuery(id+"F4.wireOp",EDGE,"E20.117.1"),sQuery(id+"F4.wireOp",EDGE,"E20.118.0")])]});
            var Q25;
            Q25=makeQuery(id+"F5.opExtrude","SWEPT_EDGE",EDGE,{"disambiguationData":[OSD([sQuery(id+"F0.wireOp",EDGE,"E1"),sQuery(id+"F0.wireOp",EDGE,"E2"),sQuery(id+"F4.wireOp",EDGE,"E20.117.0"),sQuery(id+"F4.wireOp",EDGE,"E20.117.1")])]});
            var Q26;
            Q26=makeQuery(id+"F5.opExtrude","SWEPT_EDGE",EDGE,{"disambiguationData":[OSD([sQuery(id+"F4.wireOp",EDGE,"E20.116.1"),sQuery(id+"F4.wireOp",EDGE,"E20.117.0")])]});
            var Q27;
            Q27=makeQuery(id+"F5.opExtrude","SWEPT_EDGE",EDGE,{"disambiguationData":[OSD([sQuery(id+"F0.wireOp",EDGE,"E1"),sQuery(id+"F0.wireOp",EDGE,"E2"),sQuery(id+"F4.wireOp",EDGE,"E20.116.0"),sQuery(id+"F4.wireOp",EDGE,"E20.116.1")])]});
            var Q28;
            Q28=makeQuery(id+"F5.opExtrude","SWEPT_EDGE",EDGE,{"disambiguationData":[OSD([sQuery(id+"F4.wireOp",EDGE,"E20.115.1"),sQuery(id+"F4.wireOp",EDGE,"E20.116.0")])]});
            var Q29;
            Q29=makeQuery(id+"F5.opExtrude","SWEPT_EDGE",EDGE,{"disambiguationData":[OSD([sQuery(id+"F0.wireOp",EDGE,"E1"),sQuery(id+"F0.wireOp",EDGE,"E2"),sQuery(id+"F4.wireOp",EDGE,"E20.115.0"),sQuery(id+"F4.wireOp",EDGE,"E20.115.1")])]});
            var Q30;
            Q30=makeQuery(id+"F5.opExtrude","SWEPT_EDGE",EDGE,{"disambiguationData":[OSD([sQuery(id+"F4.wireOp",EDGE,"E20.114.1"),sQuery(id+"F4.wireOp",EDGE,"E20.115.0")])]});
            var Q31;
            Q31=makeQuery(id+"F5.opExtrude","SWEPT_EDGE",EDGE,{"disambiguationData":[OSD([sQuery(id+"F0.wireOp",EDGE,"E1"),sQuery(id+"F0.wireOp",EDGE,"E2"),sQuery(id+"F4.wireOp",EDGE,"E20.114.0"),sQuery(id+"F4.wireOp",EDGE,"E20.114.1")])]});
            var Q32;
            Q32=makeQuery(id+"F5.opExtrude","SWEPT_EDGE",EDGE,{"disambiguationData":[OSD([sQuery(id+"F4.wireOp",EDGE,"E20.113.1"),sQuery(id+"F4.wireOp",EDGE,"E20.114.0")])]});
            var Q33;
            Q33=makeQuery(id+"F5.opExtrude","SWEPT_EDGE",EDGE,{"disambiguationData":[OSD([sQuery(id+"F0.wireOp",EDGE,"E1"),sQuery(id+"F0.wireOp",EDGE,"E2"),sQuery(id+"F4.wireOp",EDGE,"E20.113.0"),sQuery(id+"F4.wireOp",EDGE,"E20.113.1")])]});
            var Q34;
            Q34=makeQuery(id+"F5.opExtrude","SWEPT_EDGE",EDGE,{"disambiguationData":[OSD([sQuery(id+"F4.wireOp",EDGE,"E20.112.1"),sQuery(id+"F4.wireOp",EDGE,"E20.113.0")])]});
            var Q35;
            Q35=makeQuery(id+"F5.opExtrude","SWEPT_EDGE",EDGE,{"disambiguationData":[OSD([sQuery(id+"F0.wireOp",EDGE,"E1"),sQuery(id+"F0.wireOp",EDGE,"E2"),sQuery(id+"F4.wireOp",EDGE,"E20.112.0"),sQuery(id+"F4.wireOp",EDGE,"E20.112.1")])]});
            var Q36;
            Q36=makeQuery(id+"F5.opExtrude","SWEPT_EDGE",EDGE,{"disambiguationData":[OSD([sQuery(id+"F4.wireOp",EDGE,"E20.111.1"),sQuery(id+"F4.wireOp",EDGE,"E20.112.0")])]});
            var Q37;
            Q37=makeQuery(id+"F5.opExtrude","SWEPT_EDGE",EDGE,{"disambiguationData":[OSD([sQuery(id+"F0.wireOp",EDGE,"E1"),sQuery(id+"F0.wireOp",EDGE,"E2"),sQuery(id+"F4.wireOp",EDGE,"E20.111.0"),sQuery(id+"F4.wireOp",EDGE,"E20.111.1")])]});
            var Q38;
            Q38=makeQuery(id+"F5.opExtrude","SWEPT_EDGE",EDGE,{"disambiguationData":[OSD([sQuery(id+"F4.wireOp",EDGE,"E20.110.1"),sQuery(id+"F4.wireOp",EDGE,"E20.111.0")])]});
            var Q39;
            Q39=makeQuery(id+"F5.opExtrude","SWEPT_EDGE",EDGE,{"disambiguationData":[OSD([sQuery(id+"F0.wireOp",EDGE,"E1"),sQuery(id+"F0.wireOp",EDGE,"E2"),sQuery(id+"F4.wireOp",EDGE,"E20.110.0"),sQuery(id+"F4.wireOp",EDGE,"E20.110.1")])]});
            var Q40;
            Q40=makeQuery(id+"F5.opExtrude","SWEPT_EDGE",EDGE,{"disambiguationData":[OSD([sQuery(id+"F4.wireOp",EDGE,"E20.109.1"),sQuery(id+"F4.wireOp",EDGE,"E20.110.0")])]});
            var Q41;
            Q41=makeQuery(id+"F5.opExtrude","SWEPT_EDGE",EDGE,{"disambiguationData":[OSD([sQuery(id+"F0.wireOp",EDGE,"E1"),sQuery(id+"F0.wireOp",EDGE,"E2"),sQuery(id+"F4.wireOp",EDGE,"E20.109.0"),sQuery(id+"F4.wireOp",EDGE,"E20.109.1")])]});
            var Q42;
            Q42=makeQuery(id+"F5.opExtrude","SWEPT_EDGE",EDGE,{"disambiguationData":[OSD([sQuery(id+"F4.wireOp",EDGE,"E20.108.1"),sQuery(id+"F4.wireOp",EDGE,"E20.109.0")])]});
            var Q43;
            Q43=makeQuery(id+"F5.opExtrude","SWEPT_EDGE",EDGE,{"disambiguationData":[OSD([sQuery(id+"F0.wireOp",EDGE,"E1"),sQuery(id+"F0.wireOp",EDGE,"E2"),sQuery(id+"F4.wireOp",EDGE,"E20.108.0"),sQuery(id+"F4.wireOp",EDGE,"E20.108.1")])]});
            var Q44;
            Q44=makeQuery(id+"F5.opExtrude","SWEPT_EDGE",EDGE,{"disambiguationData":[OSD([sQuery(id+"F4.wireOp",EDGE,"E20.107.1"),sQuery(id+"F4.wireOp",EDGE,"E20.108.0")])]});
            var Q45;
            Q45=makeQuery(id+"F5.opExtrude","SWEPT_EDGE",EDGE,{"disambiguationData":[OSD([sQuery(id+"F0.wireOp",EDGE,"E1"),sQuery(id+"F0.wireOp",EDGE,"E2"),sQuery(id+"F4.wireOp",EDGE,"E20.107.0"),sQuery(id+"F4.wireOp",EDGE,"E20.107.1")])]});
            fillet(context, id + "F9", {"entities" : qUnion([Q0, Q1, Q2, Q3, Q4, Q5, Q6, Q7, Q8, Q9, Q10, Q11, Q12, Q13, Q14, Q15, Q16, Q17, Q18, Q19, Q20, Q21, Q22, Q23, Q24, Q25, Q26, Q27, Q28, Q29, Q30, Q31, Q32, Q33, Q34, Q35, Q36, Q37, Q38, Q39, Q40, Q41, Q42, Q43, Q44, Q45]), "radius" : .2 * mm, "tangentPropagation" : true, "allowEdgeOverflow" : false});
        }
    });
